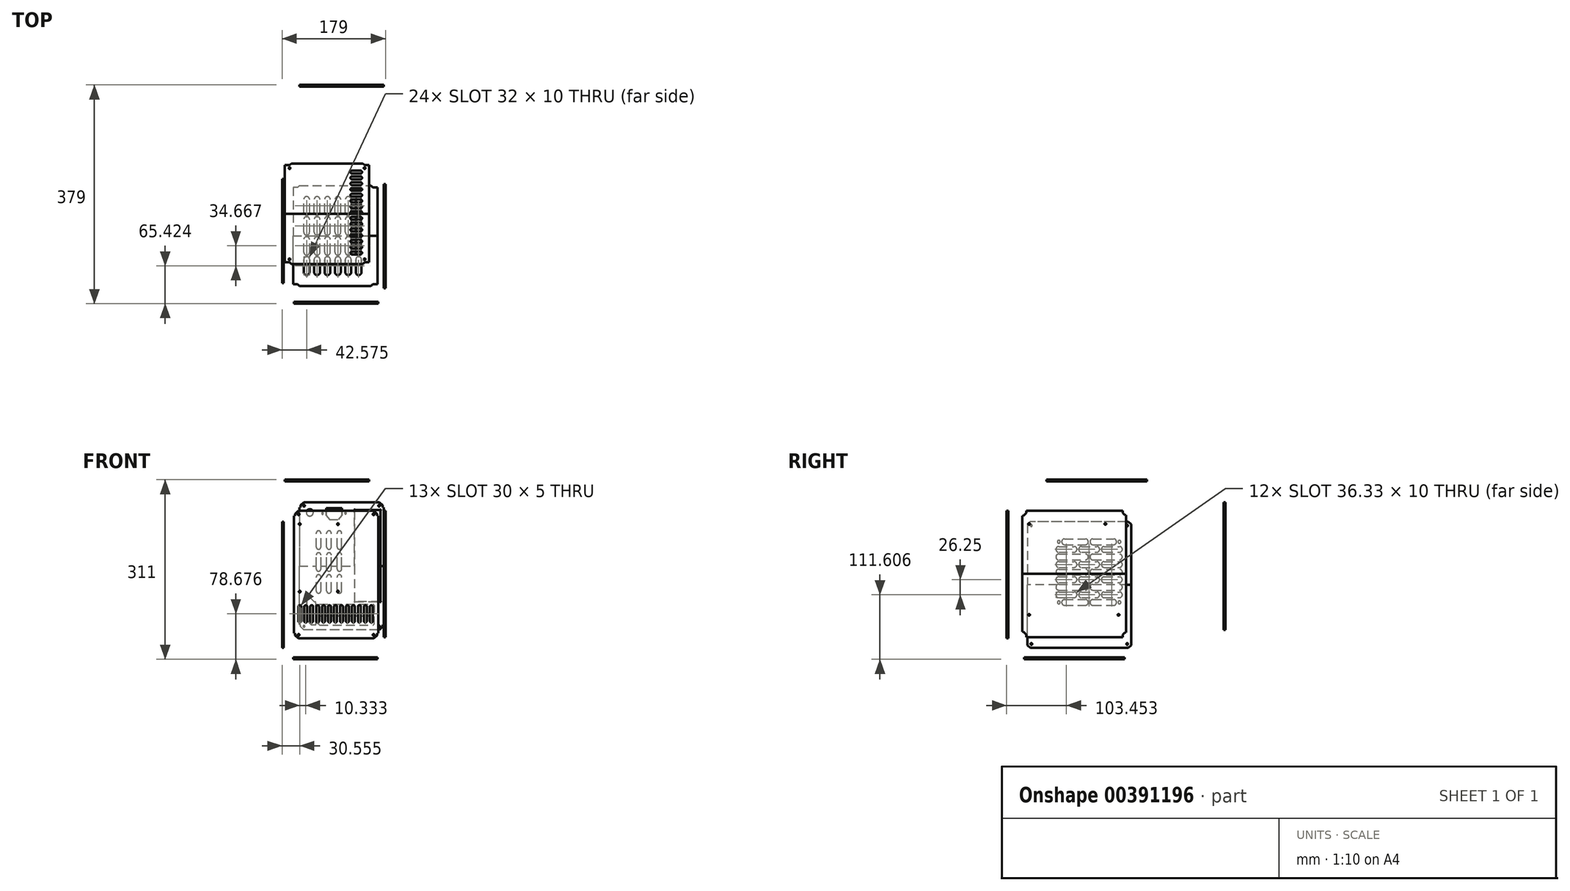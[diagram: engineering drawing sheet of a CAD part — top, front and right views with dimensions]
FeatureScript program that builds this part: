
annotation { "Feature Type Name" : "Feature", "Feature Type Description" : "" }
export const myFeature = defineFeature(function(context is Context, id is Id, definition is map)
    precondition{}
    {
        {
            var Q0;
            Q0=qCreatedBy(makeId("Front.planeOp"),FACE);
            var sketch = newSketch(context, id + "F0", { "sketchPlane" : qUnion([Q0])});
            skLineSegment(sketch, "E0.bottom", {"start": v(-75.44, 106.18) * mm, "end": v(70.56, 106.18) * mm});
            skLineSegment(sketch, "E0.top", {"start": v(-75.44, -6.32) * mm, "end": v(70.56, -6.32) * mm});
            skLineSegment(sketch, "E0.left", {"start": v(-75.44, 106.18) * mm, "end": v(-75.44, -6.32) * mm});
            skLineSegment(sketch, "E0.right", {"start": v(70.56, 106.18) * mm, "end": v(70.56, -6.32) * mm});
            skLineSegment(sketch, "E1", {"start": v(-73.44, 98.68) * mm, "end": v(-67.94, 104.18) * mm});
            skLineSegment(sketch, "E2", {"start": v(63.06, 104.18) * mm, "end": v(-67.94, 104.18) * mm});
            skLineSegment(sketch, "E3", {"start": v(63.06, 104.18) * mm, "end": v(68.56, 98.68) * mm});
            skLineSegment(sketch, "E4", {"start": v(-75.44, 98.18) * mm, "end": v(-67.44, 98.18) * mm, "construction": true});
            skCircle(sketch, "E5", {"center": v(-67.44, 98.18) * mm, "radius": 1.5 * mm});
            skLineSegment(sketch, "E6", {"start": v(70.56, 98.18) * mm, "end": v(62.56, 98.18) * mm, "construction": true});
            skCircle(sketch, "E7", {"center": v(62.56, 98.18) * mm, "radius": 1.5 * mm});
            skLineSegment(sketch, "E8", {"start": v(-73.44, 98.68) * mm, "end": v(-73.44, 95.18) * mm});
            skLineSegment(sketch, "E9", {"start": v(-73.44, 95.18) * mm, "end": v(-75.44, 95.18) * mm});
            skLineSegment(sketch, "E10", {"start": v(68.56, 98.68) * mm, "end": v(68.56, 95.18) * mm});
            skLineSegment(sketch, "E11", {"start": v(68.56, 95.18) * mm, "end": v(70.56, 95.18) * mm});
            skLineSegment(sketch, "E12", {"start": v(63.06, 104.18) * mm, "end": v(63.06, 106.18) * mm, "construction": true});
            skSolve(sketch);
        }
        {
            var Q0;
            {var subQ1=sQuery(id+"F0.wireOp",EDGE,"E0.top");Q0=makeQuery(id+"F0.imprint","IMPRINT",FACE,{"disambiguationData":[TD([[makeQuery(id+"F0.imprint","IMPRINT",EDGE,{"derivedFrom":subQ1}),1.0]])]});}
            extrude(context, id + "F1", {"entities" : qUnion([Q0]), "depth" : 3 * mm});
        }
        {
            var Q0;
            Q0=makeQuery(id+"F1.opExtrude","SWEPT_BODY",BODY,{"disambiguationData":[OSD([sQuery(id+"F0.wireOp",EDGE,"E0.bottom"),sQuery(id+"F0.wireOp",EDGE,"E0.top"),sQuery(id+"F0.wireOp",EDGE,"E0.left"),sQuery(id+"F0.wireOp",EDGE,"E0.right"),sQuery(id+"F0.wireOp",EDGE,"f4ycc0LQ-zHDD-6vh2-nqyr-j4wCRgx8H2At"),sQuery(id+"F0.wireOp",EDGE,"E1"),sQuery(id+"F0.wireOp",EDGE,"8kIEKiAh-QTEb-dtpp-JcTS-wpPMPQfBbqQd"),sQuery(id+"F0.wireOp",EDGE,"IAD0FTGy-GJaP-wMLm-guci-XfnhwucHu2uu"),sQuery(id+"F0.wireOp",EDGE,"IvHsRxJE-VIxi-RXbs-pRJC-tqeUj7lQNFDg"),sQuery(id+"F0.wireOp",EDGE,"jDx6nEBO-jJHg-Gf5S-wIms-nsZNRVFYcTxt")])]});
            var Q1;
            Q1=makeQuery(id+"F1.opExtrude","SWEPT_FACE",FACE,{"disambiguationData":[OSD([sQuery(id+"F0.wireOp",EDGE,"E0.top")])]});
            mirror(context, id + "F2", {"operationType" : NewBodyOperationType.ADD, "entities" : qUnion([Q0]), "mirrorPlane" : qUnion([Q1])});
        }
        {
            var Q0;
            {var subQ0=makeQuery(id+"F1.opExtrude","CAP_FACE",FACE,{"disambiguationData":[OSD([sQuery(id+"F0.wireOp",EDGE,"E0.bottom"),sQuery(id+"F0.wireOp",EDGE,"E0.top"),sQuery(id+"F0.wireOp",EDGE,"E0.left"),sQuery(id+"F0.wireOp",EDGE,"E0.right"),sQuery(id+"F0.wireOp",EDGE,"f4ycc0LQ-zHDD-6vh2-nqyr-j4wCRgx8H2At"),sQuery(id+"F0.wireOp",EDGE,"E1"),sQuery(id+"F0.wireOp",EDGE,"8kIEKiAh-QTEb-dtpp-JcTS-wpPMPQfBbqQd"),sQuery(id+"F0.wireOp",EDGE,"IAD0FTGy-GJaP-wMLm-guci-XfnhwucHu2uu"),sQuery(id+"F0.wireOp",EDGE,"IvHsRxJE-VIxi-RXbs-pRJC-tqeUj7lQNFDg"),sQuery(id+"F0.wireOp",EDGE,"jDx6nEBO-jJHg-Gf5S-wIms-nsZNRVFYcTxt")])],"isStart":false});Q0=makeQuery(id+"F2.boolean.opBoolean","MERGE",FACE,{"derivedFrom":[subQ0,makeQuery(id+"F2.opPattern","COPY",FACE,{"derivedFrom":subQ0,"instanceName":"1"})]});}
            var sketch = newSketch(context, id + "F3", { "sketchPlane" : qUnion([Q0])});
            skLineSegment(sketch, "E13", {"start": v(-65.44, -86.82) * mm, "end": v(-65.44, -116.82) * mm, "construction": true});
            skLineSegment(sketch, "E14.bottom", {"start": v(-65.44, 81.18) * mm, "end": v(0.76, 81.18) * mm, "construction": true});
            skLineSegment(sketch, "E14.top", {"start": v(-65.44, -35.82) * mm, "end": v(0.76, -35.82) * mm, "construction": true});
            skLineSegment(sketch, "E14.left", {"start": v(-65.44, 81.18) * mm, "end": v(-65.44, -35.82) * mm, "construction": true});
            skLineSegment(sketch, "E14.right", {"start": v(0.76, 81.18) * mm, "end": v(0.76, -35.82) * mm, "construction": true});
            skLineSegment(sketch, "E15", {"start": v(-65.44, 81.18) * mm, "end": v(-75.44, 81.18) * mm, "construction": true});
            skCircle(sketch, "E16", {"center": v(0.76, 81.18) * mm, "radius": 1.5 * mm});
            skCircle(sketch, "E17", {"center": v(-65.44, 81.18) * mm, "radius": 1.5 * mm});
            skCircle(sketch, "E18", {"center": v(-65.44, -35.82) * mm, "radius": 1.5 * mm});
            skCircle(sketch, "E19", {"center": v(0.76, -35.82) * mm, "radius": 1.5 * mm});
            skLineSegment(sketch, "E20", {"start": v(-65.44, -86.82) * mm, "end": v(-65.44, -61.82) * mm, "construction": true});
            skArc(sketch, "E21.0.startCap", {"start": v(-62.94, -86.82) * mm, "mid": v(-65.44, -89.32) * mm, "end": v(-67.94, -86.82) * mm});
            skArc(sketch, "E21.0.endCap", {"start": v(-67.94, -61.82) * mm, "mid": v(-65.44, -59.32) * mm, "end": v(-62.94, -61.82) * mm});
            skLineSegment(sketch, "E21.0.left", {"start": v(-67.94, -86.82) * mm, "end": v(-67.94, -61.82) * mm});
            skLineSegment(sketch, "E21.0.right", {"start": v(-62.94, -86.82) * mm, "end": v(-62.94, -61.82) * mm});
            skLineSegment(sketch, "E22.1.0.0", {"start": v(-55.11, -86.82) * mm, "end": v(-55.11, -61.82) * mm, "construction": true});
            skArc(sketch, "E22.1.0.1", {"start": v(-52.61, -86.82) * mm, "mid": v(-55.11, -89.32) * mm, "end": v(-57.61, -86.82) * mm});
            skArc(sketch, "E22.1.0.2", {"start": v(-57.61, -61.82) * mm, "mid": v(-55.11, -59.32) * mm, "end": v(-52.61, -61.82) * mm});
            skLineSegment(sketch, "E22.1.0.3", {"start": v(-52.61, -86.82) * mm, "end": v(-52.61, -61.82) * mm});
            skLineSegment(sketch, "E22.1.0.4", {"start": v(-57.61, -86.82) * mm, "end": v(-57.61, -61.82) * mm});
            skLineSegment(sketch, "E22.2.0.0", {"start": v(-44.78, -86.82) * mm, "end": v(-44.78, -61.82) * mm, "construction": true});
            skArc(sketch, "E22.2.0.1", {"start": v(-42.28, -86.82) * mm, "mid": v(-44.78, -89.32) * mm, "end": v(-47.28, -86.82) * mm});
            skArc(sketch, "E22.2.0.2", {"start": v(-47.28, -61.82) * mm, "mid": v(-44.78, -59.32) * mm, "end": v(-42.28, -61.82) * mm});
            skLineSegment(sketch, "E22.2.0.3", {"start": v(-42.28, -86.82) * mm, "end": v(-42.28, -61.82) * mm});
            skLineSegment(sketch, "E22.2.0.4", {"start": v(-47.28, -86.82) * mm, "end": v(-47.28, -61.82) * mm});
            skLineSegment(sketch, "E22.3.0.0", {"start": v(-34.45, -86.82) * mm, "end": v(-34.45, -61.82) * mm, "construction": true});
            skArc(sketch, "E22.3.0.1", {"start": v(-31.95, -86.82) * mm, "mid": v(-34.45, -89.32) * mm, "end": v(-36.95, -86.82) * mm});
            skArc(sketch, "E22.3.0.2", {"start": v(-36.95, -61.82) * mm, "mid": v(-34.45, -59.32) * mm, "end": v(-31.95, -61.82) * mm});
            skLineSegment(sketch, "E22.3.0.3", {"start": v(-31.95, -86.82) * mm, "end": v(-31.95, -61.82) * mm});
            skLineSegment(sketch, "E22.3.0.4", {"start": v(-36.95, -86.82) * mm, "end": v(-36.95, -61.82) * mm});
            skLineSegment(sketch, "E22.4.0.0", {"start": v(-24.11, -86.82) * mm, "end": v(-24.11, -61.82) * mm, "construction": true});
            skArc(sketch, "E22.4.0.1", {"start": v(-21.61, -86.82) * mm, "mid": v(-24.11, -89.32) * mm, "end": v(-26.61, -86.82) * mm});
            skArc(sketch, "E22.4.0.2", {"start": v(-26.61, -61.82) * mm, "mid": v(-24.11, -59.32) * mm, "end": v(-21.61, -61.82) * mm});
            skLineSegment(sketch, "E22.4.0.3", {"start": v(-21.61, -86.82) * mm, "end": v(-21.61, -61.82) * mm});
            skLineSegment(sketch, "E22.4.0.4", {"start": v(-26.61, -86.82) * mm, "end": v(-26.61, -61.82) * mm});
            skLineSegment(sketch, "E22.5.0.0", {"start": v(-13.78, -86.82) * mm, "end": v(-13.78, -61.82) * mm, "construction": true});
            skArc(sketch, "E22.5.0.1", {"start": v(-11.28, -86.82) * mm, "mid": v(-13.78, -89.32) * mm, "end": v(-16.28, -86.82) * mm});
            skArc(sketch, "E22.5.0.2", {"start": v(-16.28, -61.82) * mm, "mid": v(-13.78, -59.32) * mm, "end": v(-11.28, -61.82) * mm});
            skLineSegment(sketch, "E22.5.0.3", {"start": v(-11.28, -86.82) * mm, "end": v(-11.28, -61.82) * mm});
            skLineSegment(sketch, "E22.5.0.4", {"start": v(-16.28, -86.82) * mm, "end": v(-16.28, -61.82) * mm});
            skLineSegment(sketch, "E22.6.0.0", {"start": v(-3.45, -86.82) * mm, "end": v(-3.45, -61.82) * mm, "construction": true});
            skArc(sketch, "E22.6.0.1", {"start": v(-0.95, -86.82) * mm, "mid": v(-3.45, -89.32) * mm, "end": v(-5.95, -86.82) * mm});
            skArc(sketch, "E22.6.0.2", {"start": v(-5.95, -61.82) * mm, "mid": v(-3.45, -59.32) * mm, "end": v(-0.95, -61.82) * mm});
            skLineSegment(sketch, "E22.6.0.3", {"start": v(-0.95, -86.82) * mm, "end": v(-0.95, -61.82) * mm});
            skLineSegment(sketch, "E22.6.0.4", {"start": v(-5.95, -86.82) * mm, "end": v(-5.95, -61.82) * mm});
            skLineSegment(sketch, "E22.7.0.0", {"start": v(6.89, -86.82) * mm, "end": v(6.89, -61.82) * mm, "construction": true});
            skArc(sketch, "E22.7.0.1", {"start": v(9.39, -86.82) * mm, "mid": v(6.89, -89.32) * mm, "end": v(4.39, -86.82) * mm});
            skArc(sketch, "E22.7.0.2", {"start": v(4.39, -61.82) * mm, "mid": v(6.89, -59.32) * mm, "end": v(9.39, -61.82) * mm});
            skLineSegment(sketch, "E22.7.0.3", {"start": v(9.39, -86.82) * mm, "end": v(9.39, -61.82) * mm});
            skLineSegment(sketch, "E22.7.0.4", {"start": v(4.39, -86.82) * mm, "end": v(4.39, -61.82) * mm});
            skLineSegment(sketch, "E22.8.0.0", {"start": v(17.22, -86.82) * mm, "end": v(17.22, -61.82) * mm, "construction": true});
            skArc(sketch, "E22.8.0.1", {"start": v(19.72, -86.82) * mm, "mid": v(17.22, -89.32) * mm, "end": v(14.72, -86.82) * mm});
            skArc(sketch, "E22.8.0.2", {"start": v(14.72, -61.82) * mm, "mid": v(17.22, -59.32) * mm, "end": v(19.72, -61.82) * mm});
            skLineSegment(sketch, "E22.8.0.3", {"start": v(19.72, -86.82) * mm, "end": v(19.72, -61.82) * mm});
            skLineSegment(sketch, "E22.8.0.4", {"start": v(14.72, -86.82) * mm, "end": v(14.72, -61.82) * mm});
            skLineSegment(sketch, "E22.9.0.0", {"start": v(27.55, -86.82) * mm, "end": v(27.55, -61.82) * mm, "construction": true});
            skArc(sketch, "E22.9.0.1", {"start": v(30.05, -86.82) * mm, "mid": v(27.55, -89.32) * mm, "end": v(25.05, -86.82) * mm});
            skArc(sketch, "E22.9.0.2", {"start": v(25.05, -61.82) * mm, "mid": v(27.55, -59.32) * mm, "end": v(30.05, -61.82) * mm});
            skLineSegment(sketch, "E22.9.0.3", {"start": v(30.05, -86.82) * mm, "end": v(30.05, -61.82) * mm});
            skLineSegment(sketch, "E22.9.0.4", {"start": v(25.05, -86.82) * mm, "end": v(25.05, -61.82) * mm});
            skLineSegment(sketch, "E22.10.0.0", {"start": v(37.89, -86.82) * mm, "end": v(37.89, -61.82) * mm, "construction": true});
            skArc(sketch, "E22.10.0.1", {"start": v(40.39, -86.82) * mm, "mid": v(37.89, -89.32) * mm, "end": v(35.39, -86.82) * mm});
            skArc(sketch, "E22.10.0.2", {"start": v(35.39, -61.82) * mm, "mid": v(37.89, -59.32) * mm, "end": v(40.39, -61.82) * mm});
            skLineSegment(sketch, "E22.10.0.3", {"start": v(40.39, -86.82) * mm, "end": v(40.39, -61.82) * mm});
            skLineSegment(sketch, "E22.10.0.4", {"start": v(35.39, -86.82) * mm, "end": v(35.39, -61.82) * mm});
            skLineSegment(sketch, "E22.11.0.0", {"start": v(48.22, -86.82) * mm, "end": v(48.22, -61.82) * mm, "construction": true});
            skArc(sketch, "E22.11.0.1", {"start": v(50.72, -86.82) * mm, "mid": v(48.22, -89.32) * mm, "end": v(45.72, -86.82) * mm});
            skArc(sketch, "E22.11.0.2", {"start": v(45.72, -61.82) * mm, "mid": v(48.22, -59.32) * mm, "end": v(50.72, -61.82) * mm});
            skLineSegment(sketch, "E22.11.0.3", {"start": v(50.72, -86.82) * mm, "end": v(50.72, -61.82) * mm});
            skLineSegment(sketch, "E22.11.0.4", {"start": v(45.72, -86.82) * mm, "end": v(45.72, -61.82) * mm});
            skLineSegment(sketch, "E22.12.0.0", {"start": v(58.55, -86.82) * mm, "end": v(58.55, -61.82) * mm, "construction": true});
            skArc(sketch, "E22.12.0.1", {"start": v(61.05, -86.82) * mm, "mid": v(58.55, -89.32) * mm, "end": v(56.05, -86.82) * mm});
            skArc(sketch, "E22.12.0.2", {"start": v(56.05, -61.82) * mm, "mid": v(58.55, -59.32) * mm, "end": v(61.05, -61.82) * mm});
            skLineSegment(sketch, "E22.12.0.3", {"start": v(61.05, -86.82) * mm, "end": v(61.05, -61.82) * mm});
            skLineSegment(sketch, "E22.12.0.4", {"start": v(56.05, -86.82) * mm, "end": v(56.05, -61.82) * mm});
            skLineSegment(sketch, "E22.direction1", {"start": v(-67.94, -86.82) * mm, "end": v(-57.61, -86.82) * mm, "construction": true});
            skSolve(sketch);
        }
        {
            var Q0;
            Q0=qSketchRegion(id+"F3",true);
            extrude(context, id + "F4", {"entities" : qUnion([Q0]), "operationType" : NewBodyOperationType.REMOVE, "oppositeDirection" : true, "depth" : 3 * mm});
        }
        {
            var Q0;
            Q0=qCreatedBy(makeId("Right.planeOp"),FACE);
            cPlane(context, id + "F5", {"entities" : qUnion([Q0]), "cplaneType" : CPlaneType.OFFSET, "offset" : 80 * mm, "width" : 150 * mm, "height" : 150 * mm});
        }
        {
            var Q0;
            Q0=qCreatedBy(id+"F5.planeOp",FACE);
            var sketch = newSketch(context, id + "F6", { "sketchPlane" : qUnion([Q0])});
            skLineSegment(sketch, "E23.bottom", {"start": v(23.92, 104.5) * mm, "end": v(203.92, 104.5) * mm});
            skLineSegment(sketch, "E23.top", {"start": v(23.92, -5) * mm, "end": v(203.92, -5) * mm});
            skLineSegment(sketch, "E23.left", {"start": v(23.92, 104.5) * mm, "end": v(23.92, -5) * mm});
            skLineSegment(sketch, "E23.right", {"start": v(203.92, 104.5) * mm, "end": v(203.92, -5) * mm});
            skLineSegment(sketch, "E24", {"start": v(23.92, 95.5) * mm, "end": v(25.92, 95.5) * mm});
            skLineSegment(sketch, "E25", {"start": v(25.92, 95.5) * mm, "end": v(30.92, 100.5) * mm});
            skLineSegment(sketch, "E26", {"start": v(30.92, 100.5) * mm, "end": v(30.92, 104.5) * mm});
            skLineSegment(sketch, "E27", {"start": v(197.92, 104.5) * mm, "end": v(197.92, 100.5) * mm});
            skLineSegment(sketch, "E28", {"start": v(197.92, 100.5) * mm, "end": v(201.92, 96.5) * mm});
            skLineSegment(sketch, "E29", {"start": v(201.92, 96.5) * mm, "end": v(203.92, 96.5) * mm});
            skSolve(sketch);
        }
        {
            var Q0;
            {var subQ4=sQuery(id+"F6.wireOp",EDGE,"E23.top");Q0=makeQuery(id+"F6.imprint","IMPRINT",FACE,{"disambiguationData":[TD([[makeQuery(id+"F6.imprint","IMPRINT",EDGE,{"derivedFrom":subQ4}),1.0]])]});}
            extrude(context, id + "F7", {"entities" : qUnion([Q0]), "depth" : 3 * mm});
        }
        {
            var Q0;
            Q0=makeQuery(id+"F7.opExtrude","SWEPT_BODY",BODY,{"disambiguationData":[OSD([sQuery(id+"F6.wireOp",EDGE,"E23.bottom"),sQuery(id+"F6.wireOp",EDGE,"E23.top"),sQuery(id+"F6.wireOp",EDGE,"E23.left"),sQuery(id+"F6.wireOp",EDGE,"E23.right"),sQuery(id+"F6.wireOp",EDGE,"uhohLnhp-hqEh-HnCf-sw5P-UAyFwgDYjcBT"),sQuery(id+"F6.wireOp",EDGE,"PZ9vbapj-Vyhe-IVd5-wSIB-ihSb0FTefDFo"),sQuery(id+"F6.wireOp",EDGE,"Vy2RlQAS-aQ6k-OJzX-lqoE-WAFZ4NoHzz8E"),sQuery(id+"F6.wireOp",EDGE,"uOpGianr-bHoC-LPpd-ZrnQ-WT6fRq75YZDk"),sQuery(id+"F6.wireOp",EDGE,"ByD4MoDk-9vtG-w2Bj-nV2I-deXss6nWGu8L"),sQuery(id+"F6.wireOp",EDGE,"dErzSW6J-HGX5-GNXE-lozc-OmhnMsFbACEc"),sQuery(id+"F6.wireOp",EDGE,"oiYVu7ST-duG0-g5FE-uATR-zlAqLM0uh895"),sQuery(id+"F6.wireOp",EDGE,"fhnCciFL-T4Vn-rBCZ-nkKt-uSig2OXv9zq8")])]});
            var Q1;
            Q1=makeQuery(id+"F7.opExtrude","SWEPT_FACE",FACE,{"disambiguationData":[OSD([sQuery(id+"F6.wireOp",EDGE,"E23.top")])]});
            mirror(context, id + "F8", {"operationType" : NewBodyOperationType.ADD, "entities" : qUnion([Q0]), "mirrorPlane" : qUnion([Q1])});
        }
        {
            var Q0;
            {var subQ0=makeQuery(id+"F7.opExtrude","CAP_FACE",FACE,{"disambiguationData":[OSD([sQuery(id+"F6.wireOp",EDGE,"E23.bottom"),sQuery(id+"F6.wireOp",EDGE,"E23.top"),sQuery(id+"F6.wireOp",EDGE,"E23.left"),sQuery(id+"F6.wireOp",EDGE,"E23.right"),sQuery(id+"F6.wireOp",EDGE,"g6LnxF4V-R5jx-aabO-tbI6-ip1Ci8vFljjD"),sQuery(id+"F6.wireOp",EDGE,"agJmLhdB-riTp-nQB3-38GJ-uXkWwZ3pCfX2")])],"isStart":true});Q0=makeQuery(id+"F8.boolean.opBoolean","MERGE",FACE,{"derivedFrom":[subQ0,makeQuery(id+"F8.opPattern","COPY",FACE,{"derivedFrom":subQ0,"instanceName":"1"})]});}
            var sketch = newSketch(context, id + "F9", { "sketchPlane" : qUnion([Q0])});
            skLineSegment(sketch, "E30", {"start": v(-200.92, -82.5) * mm, "end": v(-200.92, 87.5) * mm, "construction": true});
            skLineSegment(sketch, "E31", {"start": v(-200.92, -82.5) * mm, "end": v(-30.92, -82.5) * mm, "construction": true});
            skLineSegment(sketch, "E32", {"start": v(-200.92, 87.5) * mm, "end": v(-30.92, 87.5) * mm, "construction": true});
            skLineSegment(sketch, "E33", {"start": v(-30.92, 87.5) * mm, "end": v(-30.92, -82.5) * mm, "construction": true});
            skLineSegment(sketch, "E34", {"start": v(-200.92, -76.1) * mm, "end": v(-190.72, -76.1) * mm, "construction": true});
            skCircle(sketch, "E35", {"center": v(-190.72, -76.1) * mm, "radius": 1.5 * mm});
            skLineSegment(sketch, "E36", {"start": v(-190.72, -76.1) * mm, "end": v(-35.82, -76.1) * mm, "construction": true});
            skCircle(sketch, "E37", {"center": v(-35.82, -76.1) * mm, "radius": 1.5 * mm});
            skLineSegment(sketch, "E38", {"start": v(-200.92, 81.3) * mm, "end": v(-167.92, 81.3) * mm, "construction": true});
            skCircle(sketch, "E39", {"center": v(-167.92, 81.3) * mm, "radius": 1.5 * mm});
            skLineSegment(sketch, "E40", {"start": v(-167.92, 81.3) * mm, "end": v(-35.82, 81.3) * mm, "construction": true});
            skCircle(sketch, "E41", {"center": v(-35.82, 81.3) * mm, "radius": 1.5 * mm});
            skSolve(sketch);
        }
        {
            var Q0;
            Q0=qSketchRegion(id+"F9",true);
            var Q1;
            {var subQ0=sQuery(id+"F9.wireOp",EDGE,"b6TVsvgF-kPWZ-6Ni7-LZi2-MRGtpnM4VBQ9");Q1=makeQuery(id+"F9.imprint","IMPRINT",FACE,{"disambiguationData":[TD([[makeQuery(id+"F9.imprint","IMPRINT",EDGE,{"derivedFrom":subQ0}),-1.0]])]});}
            extrude(context, id + "F10", {"entities" : qUnion([Q0, Q1]), "operationType" : NewBodyOperationType.REMOVE, "oppositeDirection" : true, "depth" : 25 * mm});
        }
        {
            var Q0;
            Q0=qCreatedBy(makeId("Right.planeOp"),FACE);
            cPlane(context, id + "F11", {"entities" : qUnion([Q0]), "cplaneType" : CPlaneType.OFFSET, "offset" : 96 * mm, "oppositeDirection" : true, "width" : 150 * mm, "height" : 150 * mm});
        }
        {
            var Q0;
            Q0=qCreatedBy(id+"F11.planeOp",FACE);
            var sketch = newSketch(context, id + "F12", { "sketchPlane" : qUnion([Q0])});
            skLineSegment(sketch, "E42.bottom", {"start": v(212.79, 85.48) * mm, "end": v(32.79, 85.48) * mm});
            skLineSegment(sketch, "E42.top", {"start": v(212.79, -24.02) * mm, "end": v(32.79, -24.02) * mm});
            skLineSegment(sketch, "E42.left", {"start": v(212.79, 85.48) * mm, "end": v(212.79, -24.02) * mm});
            skLineSegment(sketch, "E42.right", {"start": v(32.79, 85.48) * mm, "end": v(32.79, -24.02) * mm});
            skLineSegment(sketch, "E43", {"start": v(212.79, 80.48) * mm, "end": v(207.79, 85.48) * mm});
            skLineSegment(sketch, "E44", {"start": v(37.79, 85.48) * mm, "end": v(32.79, 80.48) * mm});
            skLineSegment(sketch, "E45", {"start": v(212.79, 78.48) * mm, "end": v(205.79, 78.48) * mm, "construction": true});
            skCircle(sketch, "E46", {"center": v(205.79, 78.48) * mm, "radius": 1.5 * mm});
            skLineSegment(sketch, "E47", {"start": v(32.79, 78.48) * mm, "end": v(39.79, 78.48) * mm, "construction": true});
            skCircle(sketch, "E48", {"center": v(39.79, 78.48) * mm, "radius": 1.5 * mm});
            skSolve(sketch);
        }
        {
            var Q0;
            {var subQ1=sQuery(id+"F12.wireOp",EDGE,"E42.top");Q0=makeQuery(id+"F12.imprint","IMPRINT",FACE,{"disambiguationData":[TD([[makeQuery(id+"F12.imprint","IMPRINT",EDGE,{"derivedFrom":subQ1}),-1.0]])]});}
            extrude(context, id + "F13", {"entities" : qUnion([Q0]), "depth" : 3 * mm});
        }
        {
            var Q0;
            Q0=makeQuery(id+"F13.opExtrude","SWEPT_BODY",BODY,{"disambiguationData":[OSD([sQuery(id+"F12.wireOp",EDGE,"E42.bottom"),sQuery(id+"F12.wireOp",EDGE,"E42.top"),sQuery(id+"F12.wireOp",EDGE,"E42.left"),sQuery(id+"F12.wireOp",EDGE,"E42.right"),sQuery(id+"F12.wireOp",EDGE,"E43"),sQuery(id+"F12.wireOp",EDGE,"E44")])]});
            var Q1;
            Q1=makeQuery(id+"F13.opExtrude","SWEPT_FACE",FACE,{"disambiguationData":[OSD([sQuery(id+"F12.wireOp",EDGE,"E42.top")])]});
            mirror(context, id + "F14", {"operationType" : NewBodyOperationType.ADD, "entities" : qUnion([Q0]), "mirrorPlane" : qUnion([Q1])});
        }
        {
            var Q0;
            {var subQ0=makeQuery(id+"F13.opExtrude","CAP_FACE",FACE,{"disambiguationData":[OSD([sQuery(id+"F12.wireOp",EDGE,"E42.bottom"),sQuery(id+"F12.wireOp",EDGE,"E42.top"),sQuery(id+"F12.wireOp",EDGE,"E42.left"),sQuery(id+"F12.wireOp",EDGE,"E42.right"),sQuery(id+"F12.wireOp",EDGE,"E43"),sQuery(id+"F12.wireOp",EDGE,"E44")])],"isStart":true});Q0=makeQuery(id+"F14.boolean.opBoolean","MERGE",FACE,{"derivedFrom":[subQ0,makeQuery(id+"F14.opPattern","COPY",FACE,{"derivedFrom":subQ0,"instanceName":"1"})]});}
            var sketch = newSketch(context, id + "F15", { "sketchPlane" : qUnion([Q0])});
            skLineSegment(sketch, "E49", {"start": v(-212.79, 55.48) * mm, "end": v(-192.29, 55.48) * mm, "construction": true});
            skLineSegment(sketch, "E50", {"start": v(-192.29, 55.48) * mm, "end": v(-192.29, -59.52) * mm, "construction": true});
            skLineSegment(sketch, "E51", {"start": v(-192.29, 50.48) * mm, "end": v(-182.29, 50.48) * mm, "construction": true});
            skLineSegment(sketch, "E52", {"start": v(-182.29, 50.48) * mm, "end": v(-146.29, 50.48) * mm, "construction": true});
            skLineSegment(sketch, "E53", {"start": v(-192.29, 37.36) * mm, "end": v(-165.95, 37.36) * mm, "construction": true});
            skLineSegment(sketch, "E54", {"start": v(-192.29, 24.23) * mm, "end": v(-146.29, 24.23) * mm, "construction": true});
            skLineSegment(sketch, "E55", {"start": v(-192.29, 11.1) * mm, "end": v(-165.95, 11.1) * mm, "construction": true});
            skLineSegment(sketch, "E56", {"start": v(-192.29, -2.02) * mm, "end": v(-146.29, -2.02) * mm, "construction": true});
            skLineSegment(sketch, "E57", {"start": v(-192.29, -15.14) * mm, "end": v(-165.95, -15.14) * mm, "construction": true});
            skLineSegment(sketch, "E58", {"start": v(-192.29, -28.27) * mm, "end": v(-146.29, -28.27) * mm, "construction": true});
            skLineSegment(sketch, "E59", {"start": v(-192.29, -41.4) * mm, "end": v(-165.95, -41.4) * mm, "construction": true});
            skLineSegment(sketch, "E60", {"start": v(-192.29, -54.52) * mm, "end": v(-182.29, -54.52) * mm, "construction": true});
            skLineSegment(sketch, "E61", {"start": v(-182.29, -54.52) * mm, "end": v(-146.29, -54.52) * mm, "construction": true});
            skCircle(sketch, "E62", {"center": v(-192.29, 50.48) * mm, "radius": 2.5 * mm});
            skLineSegment(sketch, "E63", {"start": v(-97.29, 50.48) * mm, "end": v(-87.29, 50.48) * mm, "construction": true});
            skPoint(sketch, "E63.endSnap0", {"position": v(-82.69, 50.48) * mm});
            skCircle(sketch, "E64", {"center": v(-87.29, 50.48) * mm, "radius": 2.5 * mm});
            skLineSegment(sketch, "E65", {"start": v(-146.29, 50.48) * mm, "end": v(-133.29, 50.48) * mm, "construction": true});
            skLineSegment(sketch, "E66", {"start": v(-133.29, 50.48) * mm, "end": v(-97.29, 50.48) * mm, "construction": true});
            skArc(sketch, "E67.0.startCap", {"start": v(-182.29, 45.48) * mm, "mid": v(-187.29, 50.48) * mm, "end": v(-182.29, 55.48) * mm});
            skArc(sketch, "E67.0.endCap", {"start": v(-146.29, 55.48) * mm, "mid": v(-141.29, 50.48) * mm, "end": v(-146.29, 45.48) * mm});
            skLineSegment(sketch, "E67.0.left", {"start": v(-182.29, 55.48) * mm, "end": v(-146.29, 55.48) * mm});
            skLineSegment(sketch, "E67.0.right", {"start": v(-182.29, 45.48) * mm, "end": v(-146.29, 45.48) * mm});
            skArc(sketch, "E67.1.startCap", {"start": v(-133.29, 45.48) * mm, "mid": v(-138.29, 50.48) * mm, "end": v(-133.29, 55.48) * mm});
            skArc(sketch, "E67.1.endCap", {"start": v(-97.29, 55.48) * mm, "mid": v(-92.29, 50.48) * mm, "end": v(-97.29, 45.48) * mm});
            skLineSegment(sketch, "E67.1.left", {"start": v(-133.29, 55.48) * mm, "end": v(-97.29, 55.48) * mm});
            skLineSegment(sketch, "E67.1.right", {"start": v(-133.29, 45.48) * mm, "end": v(-97.29, 45.48) * mm});
            skLineSegment(sketch, "E68", {"start": v(-165.95, 37.36) * mm, "end": v(-152.95, 37.36) * mm, "construction": true});
            skLineSegment(sketch, "E69", {"start": v(-152.95, 37.36) * mm, "end": v(-126.62, 37.36) * mm, "construction": true});
            skLineSegment(sketch, "E70", {"start": v(-126.62, 37.36) * mm, "end": v(-113.62, 37.36) * mm, "construction": true});
            skLineSegment(sketch, "E71", {"start": v(-113.62, 37.36) * mm, "end": v(-87.29, 37.36) * mm, "construction": true});
            skArc(sketch, "E72.0.startCap", {"start": v(-192.29, 32.36) * mm, "mid": v(-197.29, 37.36) * mm, "end": v(-192.29, 42.36) * mm});
            skArc(sketch, "E72.0.endCap", {"start": v(-165.95, 42.36) * mm, "mid": v(-160.95, 37.36) * mm, "end": v(-165.95, 32.36) * mm});
            skLineSegment(sketch, "E72.0.left", {"start": v(-192.29, 42.36) * mm, "end": v(-165.95, 42.36) * mm});
            skLineSegment(sketch, "E72.0.right", {"start": v(-192.29, 32.36) * mm, "end": v(-165.95, 32.36) * mm});
            skArc(sketch, "E72.1.startCap", {"start": v(-152.95, 32.36) * mm, "mid": v(-157.95, 37.36) * mm, "end": v(-152.95, 42.36) * mm});
            skArc(sketch, "E72.1.endCap", {"start": v(-126.62, 42.36) * mm, "mid": v(-121.62, 37.36) * mm, "end": v(-126.62, 32.36) * mm});
            skLineSegment(sketch, "E72.1.left", {"start": v(-152.95, 42.36) * mm, "end": v(-126.62, 42.36) * mm});
            skLineSegment(sketch, "E72.1.right", {"start": v(-152.95, 32.36) * mm, "end": v(-126.62, 32.36) * mm});
            skArc(sketch, "E72.2.startCap", {"start": v(-113.62, 32.36) * mm, "mid": v(-118.62, 37.36) * mm, "end": v(-113.62, 42.36) * mm});
            skArc(sketch, "E72.2.endCap", {"start": v(-87.29, 42.36) * mm, "mid": v(-82.29, 37.36) * mm, "end": v(-87.29, 32.36) * mm});
            skLineSegment(sketch, "E72.2.left", {"start": v(-113.62, 42.36) * mm, "end": v(-87.29, 42.36) * mm});
            skLineSegment(sketch, "E72.2.right", {"start": v(-113.62, 32.36) * mm, "end": v(-87.29, 32.36) * mm});
            skLineSegment(sketch, "E73", {"start": v(-146.29, 24.23) * mm, "end": v(-133.29, 24.23) * mm, "construction": true});
            skLineSegment(sketch, "E74", {"start": v(-133.29, 24.23) * mm, "end": v(-87.29, 24.23) * mm, "construction": true});
            skArc(sketch, "E75.0.startCap", {"start": v(-192.29, 19.23) * mm, "mid": v(-197.29, 24.23) * mm, "end": v(-192.29, 29.23) * mm});
            skArc(sketch, "E75.0.endCap", {"start": v(-146.29, 29.23) * mm, "mid": v(-141.29, 24.23) * mm, "end": v(-146.29, 19.23) * mm});
            skLineSegment(sketch, "E75.0.left", {"start": v(-192.29, 29.23) * mm, "end": v(-146.29, 29.23) * mm});
            skLineSegment(sketch, "E75.0.right", {"start": v(-192.29, 19.23) * mm, "end": v(-146.29, 19.23) * mm});
            skArc(sketch, "E75.1.startCap", {"start": v(-133.29, 19.23) * mm, "mid": v(-138.29, 24.23) * mm, "end": v(-133.29, 29.23) * mm});
            skArc(sketch, "E75.1.endCap", {"start": v(-87.29, 29.23) * mm, "mid": v(-82.29, 24.23) * mm, "end": v(-87.29, 19.23) * mm});
            skLineSegment(sketch, "E75.1.left", {"start": v(-133.29, 29.23) * mm, "end": v(-87.29, 29.23) * mm});
            skLineSegment(sketch, "E75.1.right", {"start": v(-133.29, 19.23) * mm, "end": v(-87.29, 19.23) * mm});
            skLineSegment(sketch, "E76", {"start": v(-165.95, 11.1) * mm, "end": v(-152.95, 11.1) * mm, "construction": true});
            skLineSegment(sketch, "E77", {"start": v(-152.95, 11.1) * mm, "end": v(-126.62, 11.1) * mm, "construction": true});
            skLineSegment(sketch, "E78", {"start": v(-126.62, 11.1) * mm, "end": v(-113.62, 11.1) * mm, "construction": true});
            skLineSegment(sketch, "E79", {"start": v(-113.62, 11.1) * mm, "end": v(-87.29, 11.1) * mm, "construction": true});
            skArc(sketch, "E80.0.startCap", {"start": v(-192.29, 6.1) * mm, "mid": v(-197.29, 11.1) * mm, "end": v(-192.29, 16.1) * mm});
            skArc(sketch, "E80.0.endCap", {"start": v(-165.95, 16.1) * mm, "mid": v(-160.95, 11.1) * mm, "end": v(-165.95, 6.1) * mm});
            skLineSegment(sketch, "E80.0.left", {"start": v(-192.29, 16.1) * mm, "end": v(-165.95, 16.1) * mm});
            skLineSegment(sketch, "E80.0.right", {"start": v(-192.29, 6.1) * mm, "end": v(-165.95, 6.1) * mm});
            skArc(sketch, "E80.1.startCap", {"start": v(-152.95, 6.1) * mm, "mid": v(-157.95, 11.1) * mm, "end": v(-152.95, 16.1) * mm});
            skArc(sketch, "E80.1.endCap", {"start": v(-126.62, 16.1) * mm, "mid": v(-121.62, 11.1) * mm, "end": v(-126.62, 6.1) * mm});
            skLineSegment(sketch, "E80.1.left", {"start": v(-152.95, 16.1) * mm, "end": v(-126.62, 16.1) * mm});
            skLineSegment(sketch, "E80.1.right", {"start": v(-152.95, 6.1) * mm, "end": v(-126.62, 6.1) * mm});
            skArc(sketch, "E80.2.startCap", {"start": v(-113.62, 6.1) * mm, "mid": v(-118.62, 11.1) * mm, "end": v(-113.62, 16.1) * mm});
            skArc(sketch, "E80.2.endCap", {"start": v(-87.29, 16.1) * mm, "mid": v(-82.29, 11.1) * mm, "end": v(-87.29, 6.1) * mm});
            skLineSegment(sketch, "E80.2.left", {"start": v(-113.62, 16.1) * mm, "end": v(-87.29, 16.1) * mm});
            skLineSegment(sketch, "E80.2.right", {"start": v(-113.62, 6.1) * mm, "end": v(-87.29, 6.1) * mm});
            skLineSegment(sketch, "E81", {"start": v(-146.29, -2.02) * mm, "end": v(-133.29, -2.02) * mm, "construction": true});
            skLineSegment(sketch, "E82", {"start": v(-133.29, -2.02) * mm, "end": v(-87.29, -2.02) * mm, "construction": true});
            skLineSegment(sketch, "E83", {"start": v(-165.95, -15.14) * mm, "end": v(-152.95, -15.14) * mm, "construction": true});
            skLineSegment(sketch, "E84", {"start": v(-152.95, -15.14) * mm, "end": v(-126.62, -15.14) * mm, "construction": true});
            skLineSegment(sketch, "E85", {"start": v(-126.62, -15.14) * mm, "end": v(-113.62, -15.14) * mm, "construction": true});
            skLineSegment(sketch, "E86", {"start": v(-113.62, -15.14) * mm, "end": v(-87.29, -15.14) * mm, "construction": true});
            skLineSegment(sketch, "E87", {"start": v(-146.29, -28.27) * mm, "end": v(-133.29, -28.27) * mm, "construction": true});
            skLineSegment(sketch, "E88", {"start": v(-133.29, -28.27) * mm, "end": v(-87.29, -28.27) * mm, "construction": true});
            skLineSegment(sketch, "E89", {"start": v(-165.95, -41.4) * mm, "end": v(-152.95, -41.4) * mm, "construction": true});
            skLineSegment(sketch, "E90", {"start": v(-152.95, -41.4) * mm, "end": v(-126.62, -41.4) * mm, "construction": true});
            skLineSegment(sketch, "E91", {"start": v(-126.62, -41.4) * mm, "end": v(-113.62, -41.4) * mm, "construction": true});
            skLineSegment(sketch, "E92", {"start": v(-113.62, -41.4) * mm, "end": v(-87.29, -41.4) * mm, "construction": true});
            skLineSegment(sketch, "E93", {"start": v(-146.29, -54.52) * mm, "end": v(-133.29, -54.52) * mm, "construction": true});
            skLineSegment(sketch, "E94", {"start": v(-133.29, -54.52) * mm, "end": v(-97.29, -54.52) * mm, "construction": true});
            skLineSegment(sketch, "E95", {"start": v(-97.29, -54.52) * mm, "end": v(-87.29, -54.52) * mm, "construction": true});
            skArc(sketch, "E96.0.startCap", {"start": v(-192.29, -7.02) * mm, "mid": v(-197.29, -2.02) * mm, "end": v(-192.29, 2.98) * mm});
            skArc(sketch, "E96.0.endCap", {"start": v(-146.29, 2.98) * mm, "mid": v(-141.29, -2.02) * mm, "end": v(-146.29, -7.02) * mm});
            skLineSegment(sketch, "E96.0.left", {"start": v(-192.29, 2.98) * mm, "end": v(-146.29, 2.98) * mm});
            skLineSegment(sketch, "E96.0.right", {"start": v(-192.29, -7.02) * mm, "end": v(-146.29, -7.02) * mm});
            skArc(sketch, "E96.1.startCap", {"start": v(-133.29, -7.02) * mm, "mid": v(-138.29, -2.02) * mm, "end": v(-133.29, 2.98) * mm});
            skArc(sketch, "E96.1.endCap", {"start": v(-87.29, 2.98) * mm, "mid": v(-82.29, -2.02) * mm, "end": v(-87.29, -7.02) * mm});
            skLineSegment(sketch, "E96.1.left", {"start": v(-133.29, 2.98) * mm, "end": v(-87.29, 2.98) * mm});
            skLineSegment(sketch, "E96.1.right", {"start": v(-133.29, -7.02) * mm, "end": v(-87.29, -7.02) * mm});
            skArc(sketch, "E96.2.startCap", {"start": v(-192.29, -20.14) * mm, "mid": v(-197.29, -15.14) * mm, "end": v(-192.29, -10.14) * mm});
            skArc(sketch, "E96.2.endCap", {"start": v(-165.95, -10.14) * mm, "mid": v(-160.95, -15.14) * mm, "end": v(-165.95, -20.14) * mm});
            skLineSegment(sketch, "E96.2.left", {"start": v(-192.29, -10.14) * mm, "end": v(-165.95, -10.14) * mm});
            skLineSegment(sketch, "E96.2.right", {"start": v(-192.29, -20.14) * mm, "end": v(-165.95, -20.14) * mm});
            skArc(sketch, "E96.3.startCap", {"start": v(-152.95, -20.14) * mm, "mid": v(-157.95, -15.14) * mm, "end": v(-152.95, -10.14) * mm});
            skArc(sketch, "E96.3.endCap", {"start": v(-126.62, -10.14) * mm, "mid": v(-121.62, -15.14) * mm, "end": v(-126.62, -20.14) * mm});
            skLineSegment(sketch, "E96.3.left", {"start": v(-152.95, -10.14) * mm, "end": v(-126.62, -10.14) * mm});
            skLineSegment(sketch, "E96.3.right", {"start": v(-152.95, -20.14) * mm, "end": v(-126.62, -20.14) * mm});
            skArc(sketch, "E96.4.startCap", {"start": v(-113.62, -20.14) * mm, "mid": v(-118.62, -15.14) * mm, "end": v(-113.62, -10.14) * mm});
            skArc(sketch, "E96.4.endCap", {"start": v(-87.29, -10.14) * mm, "mid": v(-82.29, -15.14) * mm, "end": v(-87.29, -20.14) * mm});
            skLineSegment(sketch, "E96.4.left", {"start": v(-113.62, -10.14) * mm, "end": v(-87.29, -10.14) * mm});
            skLineSegment(sketch, "E96.4.right", {"start": v(-113.62, -20.14) * mm, "end": v(-87.29, -20.14) * mm});
            skArc(sketch, "E97.0.startCap", {"start": v(-192.29, -33.27) * mm, "mid": v(-197.29, -28.27) * mm, "end": v(-192.29, -23.27) * mm});
            skArc(sketch, "E97.0.endCap", {"start": v(-146.29, -23.27) * mm, "mid": v(-141.29, -28.27) * mm, "end": v(-146.29, -33.27) * mm});
            skLineSegment(sketch, "E97.0.left", {"start": v(-192.29, -23.27) * mm, "end": v(-146.29, -23.27) * mm});
            skLineSegment(sketch, "E97.0.right", {"start": v(-192.29, -33.27) * mm, "end": v(-146.29, -33.27) * mm});
            skArc(sketch, "E97.1.startCap", {"start": v(-133.29, -33.27) * mm, "mid": v(-138.29, -28.27) * mm, "end": v(-133.29, -23.27) * mm});
            skArc(sketch, "E97.1.endCap", {"start": v(-87.29, -23.27) * mm, "mid": v(-82.29, -28.27) * mm, "end": v(-87.29, -33.27) * mm});
            skLineSegment(sketch, "E97.1.left", {"start": v(-133.29, -23.27) * mm, "end": v(-87.29, -23.27) * mm});
            skLineSegment(sketch, "E97.1.right", {"start": v(-133.29, -33.27) * mm, "end": v(-87.29, -33.27) * mm});
            skArc(sketch, "E97.2.startCap", {"start": v(-192.29, -46.4) * mm, "mid": v(-197.29, -41.4) * mm, "end": v(-192.29, -36.4) * mm});
            skArc(sketch, "E97.2.endCap", {"start": v(-165.95, -36.4) * mm, "mid": v(-160.95, -41.4) * mm, "end": v(-165.95, -46.4) * mm});
            skLineSegment(sketch, "E97.2.left", {"start": v(-192.29, -36.4) * mm, "end": v(-165.95, -36.4) * mm});
            skLineSegment(sketch, "E97.2.right", {"start": v(-192.29, -46.4) * mm, "end": v(-165.95, -46.4) * mm});
            skArc(sketch, "E97.3.startCap", {"start": v(-152.95, -46.4) * mm, "mid": v(-157.95, -41.4) * mm, "end": v(-152.95, -36.4) * mm});
            skArc(sketch, "E97.3.endCap", {"start": v(-126.62, -36.4) * mm, "mid": v(-121.62, -41.4) * mm, "end": v(-126.62, -46.4) * mm});
            skLineSegment(sketch, "E97.3.left", {"start": v(-152.95, -36.4) * mm, "end": v(-126.62, -36.4) * mm});
            skLineSegment(sketch, "E97.3.right", {"start": v(-152.95, -46.4) * mm, "end": v(-126.62, -46.4) * mm});
            skArc(sketch, "E97.4.startCap", {"start": v(-113.62, -46.4) * mm, "mid": v(-118.62, -41.4) * mm, "end": v(-113.62, -36.4) * mm});
            skArc(sketch, "E97.4.endCap", {"start": v(-87.29, -36.4) * mm, "mid": v(-82.29, -41.4) * mm, "end": v(-87.29, -46.4) * mm});
            skLineSegment(sketch, "E97.4.left", {"start": v(-113.62, -36.4) * mm, "end": v(-87.29, -36.4) * mm});
            skLineSegment(sketch, "E97.4.right", {"start": v(-113.62, -46.4) * mm, "end": v(-87.29, -46.4) * mm});
            skArc(sketch, "E97.5.startCap", {"start": v(-182.29, -59.52) * mm, "mid": v(-187.29, -54.52) * mm, "end": v(-182.29, -49.52) * mm});
            skArc(sketch, "E97.5.endCap", {"start": v(-146.29, -49.52) * mm, "mid": v(-141.29, -54.52) * mm, "end": v(-146.29, -59.52) * mm});
            skLineSegment(sketch, "E97.5.left", {"start": v(-182.29, -49.52) * mm, "end": v(-146.29, -49.52) * mm});
            skLineSegment(sketch, "E97.5.right", {"start": v(-182.29, -59.52) * mm, "end": v(-146.29, -59.52) * mm});
            skArc(sketch, "E97.6.startCap", {"start": v(-133.29, -59.52) * mm, "mid": v(-138.29, -54.52) * mm, "end": v(-133.29, -49.52) * mm});
            skArc(sketch, "E97.6.endCap", {"start": v(-97.29, -49.52) * mm, "mid": v(-92.29, -54.52) * mm, "end": v(-97.29, -59.52) * mm});
            skLineSegment(sketch, "E97.6.left", {"start": v(-133.29, -49.52) * mm, "end": v(-97.29, -49.52) * mm});
            skLineSegment(sketch, "E97.6.right", {"start": v(-133.29, -59.52) * mm, "end": v(-97.29, -59.52) * mm});
            skCircle(sketch, "E98", {"center": v(-192.29, -54.52) * mm, "radius": 2.5 * mm});
            skCircle(sketch, "E99", {"center": v(-87.29, -54.52) * mm, "radius": 2.5 * mm});
            skSolve(sketch);
        }
        {
            var Q0;
            Q0=qSketchRegion(id+"F15",true);
            var Q1;
            {var subQ0=sQuery(id+"F15.wireOp",EDGE,"eD3hBwOG-1YSv-rIqv-KxOD-YYoGhDVYBiqk");Q1=makeQuery(id+"F15.imprint","IMPRINT",FACE,{"disambiguationData":[TD([[makeQuery(id+"F15.imprint","IMPRINT",EDGE,{"derivedFrom":subQ0}),-1.0]])]});}
            extrude(context, id + "F16", {"entities" : qUnion([Q0, Q1]), "operationType" : NewBodyOperationType.REMOVE, "oppositeDirection" : true, "depth" : 25 * mm});
        }
        {
            var Q0;
            Q0=qCreatedBy(makeId("Top.planeOp"),FACE);
            cPlane(context, id + "F17", {"entities" : qUnion([Q0]), "cplaneType" : CPlaneType.OFFSET, "offset" : 155 * mm, "width" : 150 * mm, "height" : 150 * mm});
        }
        {
            var Q0;
            Q0=qCreatedBy(id+"F17.planeOp",FACE);
            var sketch = newSketch(context, id + "F18", { "sketchPlane" : qUnion([Q0])});
            skLineSegment(sketch, "E100.bottom", {"start": v(-91.02, 152.87) * mm, "end": v(54.98, 152.87) * mm});
            skLineSegment(sketch, "E100.top", {"start": v(-91.02, 65.87) * mm, "end": v(54.98, 65.87) * mm});
            skLineSegment(sketch, "E100.left", {"start": v(-91.02, 152.87) * mm, "end": v(-91.02, 65.87) * mm});
            skLineSegment(sketch, "E100.right", {"start": v(54.98, 152.87) * mm, "end": v(54.98, 65.87) * mm});
            skLineSegment(sketch, "E101", {"start": v(-80.02, 65.87) * mm, "end": v(-83.02, 68.87) * mm});
            skLineSegment(sketch, "E102", {"start": v(43.98, 65.87) * mm, "end": v(46.98, 68.87) * mm});
            skLineSegment(sketch, "E103", {"start": v(-83.02, 68.87) * mm, "end": v(-91.02, 68.87) * mm});
            skLineSegment(sketch, "E104", {"start": v(46.98, 68.87) * mm, "end": v(54.98, 68.87) * mm});
            skLineSegment(sketch, "E105", {"start": v(46.98, 65.87) * mm, "end": v(46.98, 73.87) * mm, "construction": true});
            skCircle(sketch, "E106", {"center": v(46.98, 73.87) * mm, "radius": 1.5 * mm});
            skLineSegment(sketch, "E107", {"start": v(-83.02, 65.87) * mm, "end": v(-83.02, 73.87) * mm, "construction": true});
            skCircle(sketch, "E108", {"center": v(-83.02, 73.87) * mm, "radius": 1.5 * mm});
            skSolve(sketch);
        }
        {
            var Q0;
            {var subQ1=sQuery(id+"F18.wireOp",EDGE,"E100.bottom");Q0=makeQuery(id+"F18.imprint","IMPRINT",FACE,{"disambiguationData":[TD([[makeQuery(id+"F18.imprint","IMPRINT",EDGE,{"derivedFrom":subQ1}),-1.0]])]});}
            extrude(context, id + "F19", {"entities" : qUnion([Q0]), "depth" : 3 * mm});
        }
        {
            var Q0;
            Q0=makeQuery(id+"F19.opExtrude","SWEPT_BODY",BODY,{"disambiguationData":[OSD([sQuery(id+"F18.wireOp",EDGE,"E100.bottom"),sQuery(id+"F18.wireOp",EDGE,"E100.top"),sQuery(id+"F18.wireOp",EDGE,"E100.left"),sQuery(id+"F18.wireOp",EDGE,"E100.right"),sQuery(id+"F18.wireOp",EDGE,"E101"),sQuery(id+"F18.wireOp",EDGE,"3zsQ1Kl9-2ynF-8LIN-0dku-r61PIn4XyDqG"),sQuery(id+"F18.wireOp",EDGE,"UXQkqX4z-jOis-0Iwp-P2ix-A9E3pHhtgsOQ"),sQuery(id+"F18.wireOp",EDGE,"E102"),sQuery(id+"F18.wireOp",EDGE,"LeDl9sKz-5wQR-wnus-53VY-3W6SMz2K6K2i"),sQuery(id+"F18.wireOp",EDGE,"1wH7Y6pB-1Br9-c6Mt-ri01-EdgmEcDOcEDC")])]});
            var Q1;
            Q1=makeQuery(id+"F19.opExtrude","SWEPT_FACE",FACE,{"disambiguationData":[OSD([sQuery(id+"F18.wireOp",EDGE,"E100.bottom")])]});
            mirror(context, id + "F20", {"operationType" : NewBodyOperationType.ADD, "entities" : qUnion([Q0]), "mirrorPlane" : qUnion([Q1])});
        }
        {
            var Q0;
            Q0=qCreatedBy(makeId("Top.planeOp"),FACE);
            cPlane(context, id + "F21", {"entities" : qUnion([Q0]), "cplaneType" : CPlaneType.OFFSET, "offset" : 153 * mm, "oppositeDirection" : true, "width" : 150 * mm, "height" : 150 * mm});
        }
        {
            var Q0;
            Q0=qCreatedBy(id+"F21.planeOp",FACE);
            var sketch = newSketch(context, id + "F22", { "sketchPlane" : qUnion([Q0])});
            skLineSegment(sketch, "E109.bottom", {"start": v(-76.92, 27.42) * mm, "end": v(69.08, 27.42) * mm});
            skLineSegment(sketch, "E109.top", {"start": v(-76.92, 114.42) * mm, "end": v(69.08, 114.42) * mm});
            skLineSegment(sketch, "E109.left", {"start": v(-76.92, 27.42) * mm, "end": v(-76.92, 114.42) * mm});
            skLineSegment(sketch, "E109.right", {"start": v(69.08, 27.42) * mm, "end": v(69.08, 114.42) * mm});
            skLineSegment(sketch, "E110", {"start": v(-65.92, 27.42) * mm, "end": v(-68.92, 30.42) * mm});
            skLineSegment(sketch, "E111", {"start": v(61.08, 30.42) * mm, "end": v(58.08, 27.42) * mm});
            skLineSegment(sketch, "E112", {"start": v(61.08, 30.42) * mm, "end": v(69.08, 30.42) * mm});
            skLineSegment(sketch, "E113", {"start": v(-68.92, 30.42) * mm, "end": v(-76.92, 30.42) * mm});
            skSolve(sketch);
        }
        {
            var Q0;
            {var subQ1=sQuery(id+"F22.wireOp",EDGE,"E109.top");Q0=makeQuery(id+"F22.imprint","IMPRINT",FACE,{"disambiguationData":[TD([[makeQuery(id+"F22.imprint","IMPRINT",EDGE,{"derivedFrom":subQ1}),-1.0]])]});}
            extrude(context, id + "F23", {"entities" : qUnion([Q0]), "depth" : 3 * mm});
        }
        {
            var Q0;
            Q0=makeQuery(id+"F23.opExtrude","SWEPT_BODY",BODY,{"disambiguationData":[OSD([sQuery(id+"F22.wireOp",EDGE,"E109.bottom"),sQuery(id+"F22.wireOp",EDGE,"E109.top"),sQuery(id+"F22.wireOp",EDGE,"E109.left"),sQuery(id+"F22.wireOp",EDGE,"E109.right"),sQuery(id+"F22.wireOp",EDGE,"E110"),sQuery(id+"F22.wireOp",EDGE,"dnEH7a7q-0e2G-ZF1u-gQp3-ZGx2YlrUhsfq"),sQuery(id+"F22.wireOp",EDGE,"EYcrjZ5U-B8Tu-Hvld-BROV-cSRqyUUC4nfP"),sQuery(id+"F22.wireOp",EDGE,"lcQWckg9-mZXk-lsL4-PW7S-RH1iYC4EfrxX"),sQuery(id+"F22.wireOp",EDGE,"m4YSihPu-nfU7-MdAm-Gg2Q-VAeN7eaJ9XWN"),sQuery(id+"F22.wireOp",EDGE,"E111")])]});
            var Q1;
            Q1=makeQuery(id+"F23.opExtrude","SWEPT_FACE",FACE,{"disambiguationData":[OSD([sQuery(id+"F22.wireOp",EDGE,"E109.top")])]});
            mirror(context, id + "F24", {"operationType" : NewBodyOperationType.ADD, "entities" : qUnion([Q0]), "mirrorPlane" : qUnion([Q1])});
        }
        {
            var Q0;
            Q0=qCreatedBy(makeId("Front.planeOp"),FACE);
            cPlane(context, id + "F25", {"entities" : qUnion([Q0]), "cplaneType" : CPlaneType.OFFSET, "offset" : 376 * mm, "oppositeDirection" : true, "width" : 150 * mm, "height" : 150 * mm});
        }
        {
            var Q0;
            {var subQ0=makeQuery(id+"F23.opExtrude","CAP_FACE",FACE,{"disambiguationData":[OSD([sQuery(id+"F22.wireOp",EDGE,"E109.bottom"),sQuery(id+"F22.wireOp",EDGE,"E109.top"),sQuery(id+"F22.wireOp",EDGE,"E109.left"),sQuery(id+"F22.wireOp",EDGE,"E109.right"),sQuery(id+"F22.wireOp",EDGE,"E110"),sQuery(id+"F22.wireOp",EDGE,"dnEH7a7q-0e2G-ZF1u-gQp3-ZGx2YlrUhsfq"),sQuery(id+"F22.wireOp",EDGE,"EYcrjZ5U-B8Tu-Hvld-BROV-cSRqyUUC4nfP"),sQuery(id+"F22.wireOp",EDGE,"lcQWckg9-mZXk-lsL4-PW7S-RH1iYC4EfrxX"),sQuery(id+"F22.wireOp",EDGE,"m4YSihPu-nfU7-MdAm-Gg2Q-VAeN7eaJ9XWN"),sQuery(id+"F22.wireOp",EDGE,"E111")])],"isStart":true});Q0=makeQuery(id+"F24.boolean.opBoolean","MERGE",FACE,{"derivedFrom":[subQ0,makeQuery(id+"F24.opPattern","COPY",FACE,{"derivedFrom":subQ0,"instanceName":"1"})]});}
            var sketch = newSketch(context, id + "F26", { "sketchPlane" : qUnion([Q0])});
            skLineSegment(sketch, "E114", {"start": v(-53.42, -177.42) * mm, "end": v(-53.42, -155.42) * mm, "construction": true});
            skLineSegment(sketch, "E115", {"start": v(-53.42, -155.42) * mm, "end": v(-53.42, -142.76) * mm, "construction": true});
            skLineSegment(sketch, "E116", {"start": v(-53.42, -142.76) * mm, "end": v(-53.42, -120.76) * mm, "construction": true});
            skLineSegment(sketch, "E117", {"start": v(-53.42, -120.76) * mm, "end": v(-53.42, -108.1) * mm, "construction": true});
            skLineSegment(sketch, "E118", {"start": v(-53.42, -108.1) * mm, "end": v(-53.42, -86.1) * mm, "construction": true});
            skLineSegment(sketch, "E119", {"start": v(-53.42, -86.1) * mm, "end": v(-53.42, -73.42) * mm, "construction": true});
            skLineSegment(sketch, "E120", {"start": v(-53.42, -177.42) * mm, "end": v(-53.42, -201.42) * mm, "construction": true});
            skLineSegment(sketch, "E121", {"start": v(-53.42, -73.42) * mm, "end": v(-53.42, -51.42) * mm, "construction": true});
            skLineSegment(sketch, "E122", {"start": v(-53.42, -51.42) * mm, "end": v(-53.42, -27.42) * mm, "construction": true});
            skArc(sketch, "E123.0.startCap", {"start": v(-48.42, -177.42) * mm, "mid": v(-53.42, -182.42) * mm, "end": v(-58.42, -177.42) * mm});
            skArc(sketch, "E123.0.endCap", {"start": v(-58.42, -155.42) * mm, "mid": v(-53.42, -150.42) * mm, "end": v(-48.42, -155.42) * mm});
            skLineSegment(sketch, "E123.0.left", {"start": v(-58.42, -177.42) * mm, "end": v(-58.42, -155.42) * mm});
            skLineSegment(sketch, "E123.0.right", {"start": v(-48.42, -177.42) * mm, "end": v(-48.42, -155.42) * mm});
            skArc(sketch, "E123.1.startCap", {"start": v(-48.42, -142.76) * mm, "mid": v(-53.42, -147.76) * mm, "end": v(-58.42, -142.76) * mm});
            skArc(sketch, "E123.1.endCap", {"start": v(-58.42, -120.76) * mm, "mid": v(-53.42, -115.76) * mm, "end": v(-48.42, -120.76) * mm});
            skLineSegment(sketch, "E123.1.left", {"start": v(-58.42, -142.76) * mm, "end": v(-58.42, -120.76) * mm});
            skLineSegment(sketch, "E123.1.right", {"start": v(-48.42, -142.76) * mm, "end": v(-48.42, -120.76) * mm});
            skArc(sketch, "E123.2.startCap", {"start": v(-48.42, -108.1) * mm, "mid": v(-53.42, -113.1) * mm, "end": v(-58.42, -108.1) * mm});
            skArc(sketch, "E123.2.endCap", {"start": v(-58.42, -86.1) * mm, "mid": v(-53.42, -81.1) * mm, "end": v(-48.42, -86.1) * mm});
            skLineSegment(sketch, "E123.2.left", {"start": v(-58.42, -108.1) * mm, "end": v(-58.42, -86.1) * mm});
            skLineSegment(sketch, "E123.2.right", {"start": v(-48.42, -108.1) * mm, "end": v(-48.42, -86.1) * mm});
            skArc(sketch, "E123.3.startCap", {"start": v(-48.42, -73.42) * mm, "mid": v(-53.42, -78.42) * mm, "end": v(-58.42, -73.42) * mm});
            skArc(sketch, "E123.3.endCap", {"start": v(-58.42, -51.42) * mm, "mid": v(-53.42, -46.42) * mm, "end": v(-48.42, -51.42) * mm});
            skLineSegment(sketch, "E123.3.left", {"start": v(-58.42, -73.42) * mm, "end": v(-58.42, -51.42) * mm});
            skLineSegment(sketch, "E123.3.right", {"start": v(-48.42, -73.42) * mm, "end": v(-48.42, -51.42) * mm});
            skArc(sketch, "E124.1.0.0", {"start": v(-30.42, -177.42) * mm, "mid": v(-35.42, -182.42) * mm, "end": v(-40.42, -177.42) * mm});
            skLineSegment(sketch, "E124.1.0.1", {"start": v(-30.42, -177.42) * mm, "end": v(-30.42, -155.42) * mm});
            skLineSegment(sketch, "E124.1.0.2", {"start": v(-40.42, -177.42) * mm, "end": v(-40.42, -155.42) * mm});
            skArc(sketch, "E124.1.0.3", {"start": v(-40.42, -155.42) * mm, "mid": v(-35.42, -150.42) * mm, "end": v(-30.42, -155.42) * mm});
            skArc(sketch, "E124.1.0.4", {"start": v(-30.42, -142.76) * mm, "mid": v(-35.42, -147.76) * mm, "end": v(-40.42, -142.76) * mm});
            skLineSegment(sketch, "E124.1.0.5", {"start": v(-30.42, -142.76) * mm, "end": v(-30.42, -120.76) * mm});
            skLineSegment(sketch, "E124.1.0.6", {"start": v(-40.42, -142.76) * mm, "end": v(-40.42, -120.76) * mm});
            skArc(sketch, "E124.1.0.7", {"start": v(-40.42, -120.76) * mm, "mid": v(-35.42, -115.76) * mm, "end": v(-30.42, -120.76) * mm});
            skLineSegment(sketch, "E124.1.0.8", {"start": v(-30.42, -108.1) * mm, "end": v(-30.42, -86.1) * mm});
            skArc(sketch, "E124.1.0.9", {"start": v(-30.42, -108.1) * mm, "mid": v(-35.42, -113.1) * mm, "end": v(-40.42, -108.1) * mm});
            skLineSegment(sketch, "E124.1.0.10", {"start": v(-40.42, -108.1) * mm, "end": v(-40.42, -86.1) * mm});
            skArc(sketch, "E124.1.0.11", {"start": v(-40.42, -86.1) * mm, "mid": v(-35.42, -81.1) * mm, "end": v(-30.42, -86.1) * mm});
            skArc(sketch, "E124.1.0.12", {"start": v(-30.42, -73.42) * mm, "mid": v(-35.42, -78.42) * mm, "end": v(-40.42, -73.42) * mm});
            skLineSegment(sketch, "E124.1.0.13", {"start": v(-30.42, -73.42) * mm, "end": v(-30.42, -51.42) * mm});
            skLineSegment(sketch, "E124.1.0.14", {"start": v(-40.42, -73.42) * mm, "end": v(-40.42, -51.42) * mm});
            skArc(sketch, "E124.1.0.15", {"start": v(-40.42, -51.42) * mm, "mid": v(-35.42, -46.42) * mm, "end": v(-30.42, -51.42) * mm});
            skArc(sketch, "E124.2.0.0", {"start": v(-12.42, -177.42) * mm, "mid": v(-17.42, -182.42) * mm, "end": v(-22.42, -177.42) * mm});
            skLineSegment(sketch, "E124.2.0.1", {"start": v(-12.42, -177.42) * mm, "end": v(-12.42, -155.42) * mm});
            skLineSegment(sketch, "E124.2.0.2", {"start": v(-22.42, -177.42) * mm, "end": v(-22.42, -155.42) * mm});
            skArc(sketch, "E124.2.0.3", {"start": v(-22.42, -155.42) * mm, "mid": v(-17.42, -150.42) * mm, "end": v(-12.42, -155.42) * mm});
            skArc(sketch, "E124.2.0.4", {"start": v(-12.42, -142.76) * mm, "mid": v(-17.42, -147.76) * mm, "end": v(-22.42, -142.76) * mm});
            skLineSegment(sketch, "E124.2.0.5", {"start": v(-12.42, -142.76) * mm, "end": v(-12.42, -120.76) * mm});
            skLineSegment(sketch, "E124.2.0.6", {"start": v(-22.42, -142.76) * mm, "end": v(-22.42, -120.76) * mm});
            skArc(sketch, "E124.2.0.7", {"start": v(-22.42, -120.76) * mm, "mid": v(-17.42, -115.76) * mm, "end": v(-12.42, -120.76) * mm});
            skLineSegment(sketch, "E124.2.0.8", {"start": v(-12.42, -108.1) * mm, "end": v(-12.42, -86.1) * mm});
            skArc(sketch, "E124.2.0.9", {"start": v(-12.42, -108.1) * mm, "mid": v(-17.42, -113.1) * mm, "end": v(-22.42, -108.1) * mm});
            skLineSegment(sketch, "E124.2.0.10", {"start": v(-22.42, -108.1) * mm, "end": v(-22.42, -86.1) * mm});
            skArc(sketch, "E124.2.0.11", {"start": v(-22.42, -86.1) * mm, "mid": v(-17.42, -81.1) * mm, "end": v(-12.42, -86.1) * mm});
            skArc(sketch, "E124.2.0.12", {"start": v(-12.42, -73.42) * mm, "mid": v(-17.42, -78.42) * mm, "end": v(-22.42, -73.42) * mm});
            skLineSegment(sketch, "E124.2.0.13", {"start": v(-12.42, -73.42) * mm, "end": v(-12.42, -51.42) * mm});
            skLineSegment(sketch, "E124.2.0.14", {"start": v(-22.42, -73.42) * mm, "end": v(-22.42, -51.42) * mm});
            skArc(sketch, "E124.2.0.15", {"start": v(-22.42, -51.42) * mm, "mid": v(-17.42, -46.42) * mm, "end": v(-12.42, -51.42) * mm});
            skArc(sketch, "E124.3.0.0", {"start": v(5.58, -177.42) * mm, "mid": v(0.58, -182.42) * mm, "end": v(-4.42, -177.42) * mm});
            skLineSegment(sketch, "E124.3.0.1", {"start": v(5.58, -177.42) * mm, "end": v(5.58, -155.42) * mm});
            skLineSegment(sketch, "E124.3.0.2", {"start": v(-4.42, -177.42) * mm, "end": v(-4.42, -155.42) * mm});
            skArc(sketch, "E124.3.0.3", {"start": v(-4.42, -155.42) * mm, "mid": v(0.58, -150.42) * mm, "end": v(5.58, -155.42) * mm});
            skArc(sketch, "E124.3.0.4", {"start": v(5.58, -142.76) * mm, "mid": v(0.58, -147.76) * mm, "end": v(-4.42, -142.76) * mm});
            skLineSegment(sketch, "E124.3.0.5", {"start": v(5.58, -142.76) * mm, "end": v(5.58, -120.76) * mm});
            skLineSegment(sketch, "E124.3.0.6", {"start": v(-4.42, -142.76) * mm, "end": v(-4.42, -120.76) * mm});
            skArc(sketch, "E124.3.0.7", {"start": v(-4.42, -120.76) * mm, "mid": v(0.58, -115.76) * mm, "end": v(5.58, -120.76) * mm});
            skLineSegment(sketch, "E124.3.0.8", {"start": v(5.58, -108.1) * mm, "end": v(5.58, -86.1) * mm});
            skArc(sketch, "E124.3.0.9", {"start": v(5.58, -108.1) * mm, "mid": v(0.58, -113.1) * mm, "end": v(-4.42, -108.1) * mm});
            skLineSegment(sketch, "E124.3.0.10", {"start": v(-4.42, -108.1) * mm, "end": v(-4.42, -86.1) * mm});
            skArc(sketch, "E124.3.0.11", {"start": v(-4.42, -86.1) * mm, "mid": v(0.58, -81.1) * mm, "end": v(5.58, -86.1) * mm});
            skArc(sketch, "E124.3.0.12", {"start": v(5.58, -73.42) * mm, "mid": v(0.58, -78.42) * mm, "end": v(-4.42, -73.42) * mm});
            skLineSegment(sketch, "E124.3.0.13", {"start": v(5.58, -73.42) * mm, "end": v(5.58, -51.42) * mm});
            skLineSegment(sketch, "E124.3.0.14", {"start": v(-4.42, -73.42) * mm, "end": v(-4.42, -51.42) * mm});
            skArc(sketch, "E124.3.0.15", {"start": v(-4.42, -51.42) * mm, "mid": v(0.58, -46.42) * mm, "end": v(5.58, -51.42) * mm});
            skArc(sketch, "E124.4.0.0", {"start": v(23.58, -177.42) * mm, "mid": v(18.58, -182.42) * mm, "end": v(13.58, -177.42) * mm});
            skLineSegment(sketch, "E124.4.0.1", {"start": v(23.58, -177.42) * mm, "end": v(23.58, -155.42) * mm});
            skLineSegment(sketch, "E124.4.0.2", {"start": v(13.58, -177.42) * mm, "end": v(13.58, -155.42) * mm});
            skArc(sketch, "E124.4.0.3", {"start": v(13.58, -155.42) * mm, "mid": v(18.58, -150.42) * mm, "end": v(23.58, -155.42) * mm});
            skArc(sketch, "E124.4.0.4", {"start": v(23.58, -142.76) * mm, "mid": v(18.58, -147.76) * mm, "end": v(13.58, -142.76) * mm});
            skLineSegment(sketch, "E124.4.0.5", {"start": v(23.58, -142.76) * mm, "end": v(23.58, -120.76) * mm});
            skLineSegment(sketch, "E124.4.0.6", {"start": v(13.58, -142.76) * mm, "end": v(13.58, -120.76) * mm});
            skArc(sketch, "E124.4.0.7", {"start": v(13.58, -120.76) * mm, "mid": v(18.58, -115.76) * mm, "end": v(23.58, -120.76) * mm});
            skLineSegment(sketch, "E124.4.0.8", {"start": v(23.58, -108.1) * mm, "end": v(23.58, -86.1) * mm});
            skArc(sketch, "E124.4.0.9", {"start": v(23.58, -108.1) * mm, "mid": v(18.58, -113.1) * mm, "end": v(13.58, -108.1) * mm});
            skLineSegment(sketch, "E124.4.0.10", {"start": v(13.58, -108.1) * mm, "end": v(13.58, -86.1) * mm});
            skArc(sketch, "E124.4.0.11", {"start": v(13.58, -86.1) * mm, "mid": v(18.58, -81.1) * mm, "end": v(23.58, -86.1) * mm});
            skArc(sketch, "E124.4.0.12", {"start": v(23.58, -73.42) * mm, "mid": v(18.58, -78.42) * mm, "end": v(13.58, -73.42) * mm});
            skLineSegment(sketch, "E124.4.0.13", {"start": v(23.58, -73.42) * mm, "end": v(23.58, -51.42) * mm});
            skLineSegment(sketch, "E124.4.0.14", {"start": v(13.58, -73.42) * mm, "end": v(13.58, -51.42) * mm});
            skArc(sketch, "E124.4.0.15", {"start": v(13.58, -51.42) * mm, "mid": v(18.58, -46.42) * mm, "end": v(23.58, -51.42) * mm});
            skArc(sketch, "E124.5.0.0", {"start": v(41.58, -177.42) * mm, "mid": v(36.58, -182.42) * mm, "end": v(31.58, -177.42) * mm});
            skLineSegment(sketch, "E124.5.0.1", {"start": v(41.58, -177.42) * mm, "end": v(41.58, -155.42) * mm});
            skLineSegment(sketch, "E124.5.0.2", {"start": v(31.58, -177.42) * mm, "end": v(31.58, -155.42) * mm});
            skArc(sketch, "E124.5.0.3", {"start": v(31.58, -155.42) * mm, "mid": v(36.58, -150.42) * mm, "end": v(41.58, -155.42) * mm});
            skArc(sketch, "E124.5.0.4", {"start": v(41.58, -142.76) * mm, "mid": v(36.58, -147.76) * mm, "end": v(31.58, -142.76) * mm});
            skLineSegment(sketch, "E124.5.0.5", {"start": v(41.58, -142.76) * mm, "end": v(41.58, -120.76) * mm});
            skLineSegment(sketch, "E124.5.0.6", {"start": v(31.58, -142.76) * mm, "end": v(31.58, -120.76) * mm});
            skArc(sketch, "E124.5.0.7", {"start": v(31.58, -120.76) * mm, "mid": v(36.58, -115.76) * mm, "end": v(41.58, -120.76) * mm});
            skLineSegment(sketch, "E124.5.0.8", {"start": v(41.58, -108.1) * mm, "end": v(41.58, -86.1) * mm});
            skArc(sketch, "E124.5.0.9", {"start": v(41.58, -108.1) * mm, "mid": v(36.58, -113.1) * mm, "end": v(31.58, -108.1) * mm});
            skLineSegment(sketch, "E124.5.0.10", {"start": v(31.58, -108.1) * mm, "end": v(31.58, -86.1) * mm});
            skArc(sketch, "E124.5.0.11", {"start": v(31.58, -86.1) * mm, "mid": v(36.58, -81.1) * mm, "end": v(41.58, -86.1) * mm});
            skArc(sketch, "E124.5.0.12", {"start": v(41.58, -73.42) * mm, "mid": v(36.58, -78.42) * mm, "end": v(31.58, -73.42) * mm});
            skLineSegment(sketch, "E124.5.0.13", {"start": v(41.58, -73.42) * mm, "end": v(41.58, -51.42) * mm});
            skLineSegment(sketch, "E124.5.0.14", {"start": v(31.58, -73.42) * mm, "end": v(31.58, -51.42) * mm});
            skArc(sketch, "E124.5.0.15", {"start": v(31.58, -51.42) * mm, "mid": v(36.58, -46.42) * mm, "end": v(41.58, -51.42) * mm});
            skLineSegment(sketch, "E124.direction1", {"start": v(-58.42, -177.42) * mm, "end": v(-40.42, -177.42) * mm, "construction": true});
            skSolve(sketch);
        }
        {
            var Q0;
            Q0=qSketchRegion(id+"F26",true);
            extrude(context, id + "F27", {"entities" : qUnion([Q0]), "operationType" : NewBodyOperationType.REMOVE, "oppositeDirection" : true, "depth" : 25 * mm});
        }
        {
            var Q0;
            Q0=qCreatedBy(id+"F25.planeOp",FACE);
            var sketch = newSketch(context, id + "F28", { "sketchPlane" : qUnion([Q0])});
            skLineSegment(sketch, "E125.bottom", {"start": v(-66, 121) * mm, "end": v(80, 121) * mm});
            skLineSegment(sketch, "E125.top", {"start": v(-66, 8.5) * mm, "end": v(80, 8.5) * mm});
            skLineSegment(sketch, "E125.left", {"start": v(-66, 121) * mm, "end": v(-66, 8.5) * mm});
            skLineSegment(sketch, "E125.right", {"start": v(80, 121) * mm, "end": v(80, 8.5) * mm});
            skLineSegment(sketch, "E126", {"start": v(-64, 113.5) * mm, "end": v(-58.5, 119) * mm});
            skLineSegment(sketch, "E127", {"start": v(72, 121) * mm, "end": v(72, 113) * mm, "construction": true});
            skCircle(sketch, "E128", {"center": v(72, 113) * mm, "radius": 1.5 * mm});
            skLineSegment(sketch, "E129", {"start": v(-58, 121) * mm, "end": v(-58, 113) * mm, "construction": true});
            skCircle(sketch, "E130", {"center": v(-58, 113) * mm, "radius": 1.5 * mm});
            skLineSegment(sketch, "E131", {"start": v(78, 113.5) * mm, "end": v(72.5, 119) * mm});
            skLineSegment(sketch, "E132", {"start": v(72.5, 119) * mm, "end": v(-58.5, 119) * mm});
            skLineSegment(sketch, "E133", {"start": v(78, 113.5) * mm, "end": v(78, 110) * mm});
            skLineSegment(sketch, "E134", {"start": v(78, 110) * mm, "end": v(80, 110) * mm});
            skLineSegment(sketch, "E135", {"start": v(-64, 113.5) * mm, "end": v(-64, 110) * mm});
            skLineSegment(sketch, "E136", {"start": v(-64, 110) * mm, "end": v(-66, 110) * mm});
            skSolve(sketch);
        }
        {
            var Q0;
            {var subQ1=sQuery(id+"F28.wireOp",EDGE,"E125.top");Q0=makeQuery(id+"F28.imprint","IMPRINT",FACE,{"disambiguationData":[TD([[makeQuery(id+"F28.imprint","IMPRINT",EDGE,{"derivedFrom":subQ1}),1.0]])]});}
            extrude(context, id + "F29", {"entities" : qUnion([Q0]), "depth" : 3 * mm});
        }
        {
            var Q0;
            Q0=makeQuery(id+"F29.opExtrude","SWEPT_BODY",BODY,{"disambiguationData":[OSD([sQuery(id+"F28.wireOp",EDGE,"E125.bottom"),sQuery(id+"F28.wireOp",EDGE,"E125.top"),sQuery(id+"F28.wireOp",EDGE,"E125.left"),sQuery(id+"F28.wireOp",EDGE,"E125.right"),sQuery(id+"F28.wireOp",EDGE,"88c43418-5c0f-4f09-8127-112137b7eb87"),sQuery(id+"F28.wireOp",EDGE,"E126"),sQuery(id+"F28.wireOp",EDGE,"ccf2e9e3-9b64-4f2a-9f18-310bc790516a"),sQuery(id+"F28.wireOp",EDGE,"c5f426b9-73f2-4868-9408-4cfd947a191f"),sQuery(id+"F28.wireOp",EDGE,"cd8d91dd-9a42-4ae4-8430-5a7eccad3886"),sQuery(id+"F28.wireOp",EDGE,"f1dcae7c-8bd8-43e5-b7b1-ff3532f110ef")])]});
            var Q1;
            Q1=makeQuery(id+"F29.opExtrude","SWEPT_FACE",FACE,{"disambiguationData":[OSD([sQuery(id+"F28.wireOp",EDGE,"E125.top")])]});
            mirror(context, id + "F30", {"operationType" : NewBodyOperationType.ADD, "entities" : qUnion([Q0]), "mirrorPlane" : qUnion([Q1])});
        }
        {
            var Q0;
            {var subQ0=makeQuery(id+"F29.opExtrude","CAP_FACE",FACE,{"disambiguationData":[OSD([sQuery(id+"F28.wireOp",EDGE,"E125.bottom"),sQuery(id+"F28.wireOp",EDGE,"E125.top"),sQuery(id+"F28.wireOp",EDGE,"E125.left"),sQuery(id+"F28.wireOp",EDGE,"E125.right"),sQuery(id+"F28.wireOp",EDGE,"88c43418-5c0f-4f09-8127-112137b7eb87"),sQuery(id+"F28.wireOp",EDGE,"E126"),sQuery(id+"F28.wireOp",EDGE,"ccf2e9e3-9b64-4f2a-9f18-310bc790516a"),sQuery(id+"F28.wireOp",EDGE,"c5f426b9-73f2-4868-9408-4cfd947a191f"),sQuery(id+"F28.wireOp",EDGE,"cd8d91dd-9a42-4ae4-8430-5a7eccad3886"),sQuery(id+"F28.wireOp",EDGE,"f1dcae7c-8bd8-43e5-b7b1-ff3532f110ef")])],"isStart":true});Q0=makeQuery(id+"F30.boolean.opBoolean","MERGE",FACE,{"derivedFrom":[subQ0,makeQuery(id+"F30.opPattern","COPY",FACE,{"derivedFrom":subQ0,"instanceName":"1"})]});}
            var sketch = newSketch(context, id + "F31", { "sketchPlane" : qUnion([Q0])});
            skLineSegment(sketch, "E137", {"start": v(-72, 103) * mm, "end": v(-72, -67) * mm, "construction": true});
            skLineSegment(sketch, "E138", {"start": v(-72, -67) * mm, "end": v(-80, -67) * mm, "construction": true});
            skLineSegment(sketch, "E139", {"start": v(-72, -65.7) * mm, "end": v(-63.9, -65.7) * mm, "construction": true});
            skLineSegment(sketch, "E140.bottom", {"start": v(-63.9, -73.65) * mm, "end": v(33.1, -73.65) * mm});
            skLineSegment(sketch, "E140.top", {"start": v(-63.9, -57.75) * mm, "end": v(33.1, -57.75) * mm});
            skLineSegment(sketch, "E140.left", {"start": v(-63.9, -73.65) * mm, "end": v(-63.9, -57.75) * mm});
            skLineSegment(sketch, "E140.right", {"start": v(33.1, -73.65) * mm, "end": v(33.1, -57.75) * mm});
            skLineSegment(sketch, "E141.bottom", {"start": v(-63.9, -78.05) * mm, "end": v(33.1, -78.05) * mm});
            skLineSegment(sketch, "E141.top", {"start": v(-63.9, -93.95) * mm, "end": v(33.1, -93.95) * mm});
            skLineSegment(sketch, "E141.left", {"start": v(-63.9, -78.05) * mm, "end": v(-63.9, -93.95) * mm});
            skLineSegment(sketch, "E141.right", {"start": v(33.1, -78.05) * mm, "end": v(33.1, -93.95) * mm});
            skLineSegment(sketch, "E142", {"start": v(33.1, -78.05) * mm, "end": v(33.1, -73.65) * mm, "construction": true});
            skLineSegment(sketch, "E143.bottom", {"start": v(-29.6, 105.6) * mm, "end": v(-74.3, 105.6) * mm});
            skLineSegment(sketch, "E144", {"start": v(-74.3, 105.6) * mm, "end": v(-74.3, -53.4) * mm});
            skLineSegment(sketch, "E145", {"start": v(-74.3, -53.4) * mm, "end": v(-29.6, -53.4) * mm});
            skLineSegment(sketch, "E146", {"start": v(-29.6, -53.4) * mm, "end": v(-29.6, 105.6) * mm});
            skArc(sketch, "E147", {"start": v(-73.55, 105.6) * mm, "mid": v(-74.83, 106.13) * mm, "end": v(-74.3, 104.85) * mm});
            skArc(sketch, "E148", {"start": v(-29.6, 104.85) * mm, "mid": v(-29.07, 106.13) * mm, "end": v(-30.35, 105.6) * mm});
            skArc(sketch, "E149", {"start": v(-30.35, -53.32) * mm, "mid": v(-29.1, -53.96) * mm, "end": v(-29.6, -52.65) * mm});
            skArc(sketch, "E150", {"start": v(-74.3, -52.65) * mm, "mid": v(-74.83, -53.93) * mm, "end": v(-73.55, -53.4) * mm});
            skLineSegment(sketch, "E151", {"start": v(37.5, -53.25) * mm, "end": v(37.5, -93.25) * mm});
            skLineSegment(sketch, "E152", {"start": v(33.1, -57.75) * mm, "end": v(37.5, -57.75) * mm, "construction": true});
            skLineSegment(sketch, "E153", {"start": v(37.5, -93.25) * mm, "end": v(45.5, -93.25) * mm});
            skLineSegment(sketch, "E154", {"start": v(45.5, -93.25) * mm, "end": v(53.5, -85.25) * mm});
            skLineSegment(sketch, "E155", {"start": v(53.5, -85.25) * mm, "end": v(53.5, -43.25) * mm});
            skLineSegment(sketch, "E156", {"start": v(37.5, -53.25) * mm, "end": v(40.5, -53.25) * mm});
            skLineSegment(sketch, "E157", {"start": v(40.5, -53.25) * mm, "end": v(50.5, -43.25) * mm});
            skLineSegment(sketch, "E158", {"start": v(50.5, -43.25) * mm, "end": v(53.5, -43.25) * mm});
            skLineSegment(sketch, "E159", {"start": v(-72.5, -102) * mm, "end": v(-80, -102) * mm, "construction": true});
            skSolve(sketch);
        }
        {
            var Q0;
            {var subQ0=makeQuery(id+"F29.opExtrude","CAP_FACE",FACE,{"disambiguationData":[OSD([sQuery(id+"F28.wireOp",EDGE,"E125.bottom"),sQuery(id+"F28.wireOp",EDGE,"E125.top"),sQuery(id+"F28.wireOp",EDGE,"E125.left"),sQuery(id+"F28.wireOp",EDGE,"E125.right"),sQuery(id+"F28.wireOp",EDGE,"88c43418-5c0f-4f09-8127-112137b7eb87"),sQuery(id+"F28.wireOp",EDGE,"E126"),sQuery(id+"F28.wireOp",EDGE,"ccf2e9e3-9b64-4f2a-9f18-310bc790516a"),sQuery(id+"F28.wireOp",EDGE,"c5f426b9-73f2-4868-9408-4cfd947a191f"),sQuery(id+"F28.wireOp",EDGE,"cd8d91dd-9a42-4ae4-8430-5a7eccad3886"),sQuery(id+"F28.wireOp",EDGE,"f1dcae7c-8bd8-43e5-b7b1-ff3532f110ef")])],"isStart":true});Q0=makeQuery(id+"F30.boolean.opBoolean","MERGE",FACE,{"derivedFrom":[subQ0,makeQuery(id+"F30.opPattern","COPY",FACE,{"derivedFrom":subQ0,"instanceName":"1"})]});}
            var sketch = newSketch(context, id + "F32", { "sketchPlane" : qUnion([Q0])});
            skLineSegment(sketch, "E160", {"start": v(-3.25, 65.5) * mm, "end": v(-3.25, 41.5) * mm, "construction": true});
            skLineSegment(sketch, "E161", {"start": v(-3.25, 41.5) * mm, "end": v(-3.25, 27.5) * mm, "construction": true});
            skLineSegment(sketch, "E162", {"start": v(-3.25, 27.5) * mm, "end": v(-3.25, 3.5) * mm, "construction": true});
            skLineSegment(sketch, "E163", {"start": v(-3.25, 3.5) * mm, "end": v(-3.25, -10.5) * mm, "construction": true});
            skLineSegment(sketch, "E164", {"start": v(-3.25, -10.5) * mm, "end": v(-3.25, -34.5) * mm, "construction": true});
            skArc(sketch, "E165.0.startCap", {"start": v(-7.25, 65.5) * mm, "mid": v(-3.25, 69.5) * mm, "end": v(0.75, 65.5) * mm});
            skArc(sketch, "E165.0.endCap", {"start": v(0.75, 41.5) * mm, "mid": v(-3.25, 37.5) * mm, "end": v(-7.25, 41.5) * mm});
            skLineSegment(sketch, "E165.0.left", {"start": v(0.75, 65.5) * mm, "end": v(0.75, 41.5) * mm});
            skLineSegment(sketch, "E165.0.right", {"start": v(-7.25, 65.5) * mm, "end": v(-7.25, 41.5) * mm});
            skArc(sketch, "E165.1.startCap", {"start": v(-7.25, 27.5) * mm, "mid": v(-3.25, 31.5) * mm, "end": v(0.75, 27.5) * mm});
            skArc(sketch, "E165.1.endCap", {"start": v(0.75, 3.5) * mm, "mid": v(-3.25, -0.5) * mm, "end": v(-7.25, 3.5) * mm});
            skLineSegment(sketch, "E165.1.left", {"start": v(0.75, 27.5) * mm, "end": v(0.75, 3.5) * mm});
            skLineSegment(sketch, "E165.1.right", {"start": v(-7.25, 27.5) * mm, "end": v(-7.25, 3.5) * mm});
            skArc(sketch, "E165.2.startCap", {"start": v(-7.25, -10.5) * mm, "mid": v(-3.25, -6.5) * mm, "end": v(0.75, -10.5) * mm});
            skArc(sketch, "E165.2.endCap", {"start": v(0.75, -34.5) * mm, "mid": v(-3.25, -38.5) * mm, "end": v(-7.25, -34.5) * mm});
            skLineSegment(sketch, "E165.2.left", {"start": v(0.75, -10.5) * mm, "end": v(0.75, -34.5) * mm});
            skLineSegment(sketch, "E165.2.right", {"start": v(-7.25, -10.5) * mm, "end": v(-7.25, -34.5) * mm});
            skLineSegment(sketch, "E166.1.0.0", {"start": v(10.75, 27.5) * mm, "end": v(10.75, 3.5) * mm});
            skArc(sketch, "E166.1.0.1", {"start": v(10.75, -10.5) * mm, "mid": v(14.75, -6.5) * mm, "end": v(18.75, -10.5) * mm});
            skArc(sketch, "E166.1.0.3", {"start": v(10.75, 65.5) * mm, "mid": v(14.75, 69.5) * mm, "end": v(18.75, 65.5) * mm});
            skLineSegment(sketch, "E166.1.0.4", {"start": v(10.75, -10.5) * mm, "end": v(10.75, -34.5) * mm});
            skArc(sketch, "E166.1.0.5", {"start": v(10.75, 27.5) * mm, "mid": v(14.75, 31.5) * mm, "end": v(18.75, 27.5) * mm});
            skArc(sketch, "E166.1.0.6", {"start": v(18.75, -34.5) * mm, "mid": v(14.75, -38.5) * mm, "end": v(10.75, -34.5) * mm});
            skArc(sketch, "E166.1.0.7", {"start": v(18.75, 3.5) * mm, "mid": v(14.75, -0.5) * mm, "end": v(10.75, 3.5) * mm});
            skLineSegment(sketch, "E166.1.0.11", {"start": v(14.75, -10.5) * mm, "end": v(14.75, -34.5) * mm, "construction": true});
            skLineSegment(sketch, "E166.1.0.12", {"start": v(14.75, 3.5) * mm, "end": v(14.75, -10.5) * mm, "construction": true});
            skLineSegment(sketch, "E166.1.0.13", {"start": v(14.75, 27.5) * mm, "end": v(14.75, 3.5) * mm, "construction": true});
            skLineSegment(sketch, "E166.1.0.14", {"start": v(14.75, 41.5) * mm, "end": v(14.75, 27.5) * mm, "construction": true});
            skLineSegment(sketch, "E166.1.0.15", {"start": v(14.75, 65.5) * mm, "end": v(14.75, 41.5) * mm, "construction": true});
            skLineSegment(sketch, "E166.1.0.16", {"start": v(18.75, 27.5) * mm, "end": v(18.75, 3.5) * mm});
            skLineSegment(sketch, "E166.1.0.20", {"start": v(10.75, 65.5) * mm, "end": v(10.75, 41.5) * mm});
            skLineSegment(sketch, "E166.1.0.21", {"start": v(18.75, 65.5) * mm, "end": v(18.75, 41.5) * mm});
            skArc(sketch, "E166.1.0.22", {"start": v(18.75, 41.5) * mm, "mid": v(14.75, 37.5) * mm, "end": v(10.75, 41.5) * mm});
            skLineSegment(sketch, "E166.1.0.23", {"start": v(18.75, -10.5) * mm, "end": v(18.75, -34.5) * mm});
            skLineSegment(sketch, "E166.2.0.0", {"start": v(28.75, 27.5) * mm, "end": v(28.75, 3.5) * mm});
            skArc(sketch, "E166.2.0.1", {"start": v(28.75, -10.5) * mm, "mid": v(32.75, -6.5) * mm, "end": v(36.75, -10.5) * mm});
            skArc(sketch, "E166.2.0.3", {"start": v(28.75, 65.5) * mm, "mid": v(32.75, 69.5) * mm, "end": v(36.75, 65.5) * mm});
            skLineSegment(sketch, "E166.2.0.4", {"start": v(28.75, -10.5) * mm, "end": v(28.75, -34.5) * mm});
            skArc(sketch, "E166.2.0.5", {"start": v(28.75, 27.5) * mm, "mid": v(32.75, 31.5) * mm, "end": v(36.75, 27.5) * mm});
            skArc(sketch, "E166.2.0.6", {"start": v(36.75, -34.5) * mm, "mid": v(32.75, -38.5) * mm, "end": v(28.75, -34.5) * mm});
            skArc(sketch, "E166.2.0.7", {"start": v(36.75, 3.5) * mm, "mid": v(32.75, -0.5) * mm, "end": v(28.75, 3.5) * mm});
            skLineSegment(sketch, "E166.2.0.11", {"start": v(32.75, -10.5) * mm, "end": v(32.75, -34.5) * mm, "construction": true});
            skLineSegment(sketch, "E166.2.0.12", {"start": v(32.75, 3.5) * mm, "end": v(32.75, -10.5) * mm, "construction": true});
            skLineSegment(sketch, "E166.2.0.13", {"start": v(32.75, 27.5) * mm, "end": v(32.75, 3.5) * mm, "construction": true});
            skLineSegment(sketch, "E166.2.0.14", {"start": v(32.75, 41.5) * mm, "end": v(32.75, 27.5) * mm, "construction": true});
            skLineSegment(sketch, "E166.2.0.15", {"start": v(32.75, 65.5) * mm, "end": v(32.75, 41.5) * mm, "construction": true});
            skLineSegment(sketch, "E166.2.0.16", {"start": v(36.75, 27.5) * mm, "end": v(36.75, 3.5) * mm});
            skLineSegment(sketch, "E166.2.0.20", {"start": v(28.75, 65.5) * mm, "end": v(28.75, 41.5) * mm});
            skLineSegment(sketch, "E166.2.0.21", {"start": v(36.75, 65.5) * mm, "end": v(36.75, 41.5) * mm});
            skArc(sketch, "E166.2.0.22", {"start": v(36.75, 41.5) * mm, "mid": v(32.75, 37.5) * mm, "end": v(28.75, 41.5) * mm});
            skLineSegment(sketch, "E166.2.0.23", {"start": v(36.75, -10.5) * mm, "end": v(36.75, -34.5) * mm});
            skLineSegment(sketch, "E166.direction1", {"start": v(-7.25, -34.5) * mm, "end": v(10.75, -34.5) * mm, "construction": true});
            skLineSegment(sketch, "E167", {"start": v(-7.75, 109) * mm, "end": v(19.75, 109) * mm});
            skLineSegment(sketch, "E168", {"start": v(-7.75, 109) * mm, "end": v(-7.75, 96) * mm});
            skLineSegment(sketch, "E169", {"start": v(-7.75, 96) * mm, "end": v(-7.75, 89.2) * mm, "construction": true});
            skLineSegment(sketch, "E170", {"start": v(-7.75, 89.2) * mm, "end": v(-2, 89.2) * mm, "construction": true});
            skLineSegment(sketch, "E171", {"start": v(-2, 89.2) * mm, "end": v(14, 89.2) * mm});
            skLineSegment(sketch, "E172", {"start": v(14, 89.2) * mm, "end": v(19.75, 89.2) * mm, "construction": true});
            skLineSegment(sketch, "E173", {"start": v(19.75, 89.2) * mm, "end": v(19.75, 96) * mm, "construction": true});
            skLineSegment(sketch, "E174", {"start": v(19.75, 96) * mm, "end": v(19.75, 109) * mm});
            skLineSegment(sketch, "E175", {"start": v(-7.75, 96) * mm, "end": v(-2, 89.2) * mm});
            skLineSegment(sketch, "E176", {"start": v(14, 89.2) * mm, "end": v(19.75, 96) * mm});
            skLineSegment(sketch, "E177", {"start": v(6, 89.2) * mm, "end": v(6, 109) * mm, "construction": true});
            skLineSegment(sketch, "E178", {"start": v(19.75, 99.6) * mm, "end": v(25.95, 99.6) * mm, "construction": true});
            skLineSegment(sketch, "E179", {"start": v(-7.75, 100) * mm, "end": v(-13.95, 100) * mm, "construction": true});
            skCircle(sketch, "E180", {"center": v(25.95, 99.6) * mm, "radius": 1.5 * mm});
            skCircle(sketch, "E181", {"center": v(-13.95, 100) * mm, "radius": 1.5 * mm});
            skLineSegment(sketch, "E182", {"start": v(6, 109) * mm, "end": v(6, 119) * mm, "construction": true});
            skLineSegment(sketch, "E183", {"start": v(48, 119) * mm, "end": v(48, 101) * mm, "construction": true});
            skLineSegment(sketch, "E184", {"start": v(48, 101) * mm, "end": v(66, 101) * mm, "construction": true});
            skCircle(sketch, "E185", {"center": v(48, 101) * mm, "radius": 6 * mm});
            skSolve(sketch);
        }
        {
            var Q0;
            Q0=qSketchRegion(id+"F31",true);
            var Q1;
            Q1=qSketchRegion(id+"F32",true);
            extrude(context, id + "F33", {"entities" : qUnion([Q0, Q1]), "operationType" : NewBodyOperationType.REMOVE, "oppositeDirection" : true, "depth" : 25 * mm});
        }
        {
            var Q0;
            Q0=makeQuery(id+"F33.boolean.opBoolean","COPY",EDGE,{"derivedFrom":makeQuery(id+"F33.opExtrude","SWEPT_EDGE",EDGE,{"disambiguationData":[OSD([sQuery(id+"F31.wireOp",EDGE,"E140.top"),sQuery(id+"F31.wireOp",EDGE,"E140.left")])]})});
            var Q1;
            Q1=makeQuery(id+"F33.boolean.opBoolean","COPY",EDGE,{"derivedFrom":makeQuery(id+"F33.opExtrude","SWEPT_EDGE",EDGE,{"disambiguationData":[OSD([sQuery(id+"F31.wireOp",EDGE,"E140.bottom"),sQuery(id+"F31.wireOp",EDGE,"E140.left")])]})});
            var Q2;
            Q2=makeQuery(id+"F33.boolean.opBoolean","COPY",EDGE,{"derivedFrom":makeQuery(id+"F33.opExtrude","SWEPT_EDGE",EDGE,{"disambiguationData":[OSD([sQuery(id+"F31.wireOp",EDGE,"E141.bottom"),sQuery(id+"F31.wireOp",EDGE,"E141.left")])]})});
            var Q3;
            Q3=makeQuery(id+"F33.boolean.opBoolean","COPY",EDGE,{"derivedFrom":makeQuery(id+"F33.opExtrude","SWEPT_EDGE",EDGE,{"disambiguationData":[OSD([sQuery(id+"F31.wireOp",EDGE,"E141.top"),sQuery(id+"F31.wireOp",EDGE,"E141.left")])]})});
            var Q4;
            Q4=makeQuery(id+"F33.boolean.opBoolean","COPY",EDGE,{"derivedFrom":makeQuery(id+"F33.opExtrude","SWEPT_EDGE",EDGE,{"disambiguationData":[OSD([sQuery(id+"F31.wireOp",EDGE,"E141.top"),sQuery(id+"F31.wireOp",EDGE,"E141.right")])]})});
            var Q5;
            Q5=makeQuery(id+"F33.boolean.opBoolean","COPY",EDGE,{"derivedFrom":makeQuery(id+"F33.opExtrude","SWEPT_EDGE",EDGE,{"disambiguationData":[OSD([sQuery(id+"F31.wireOp",EDGE,"E141.bottom"),sQuery(id+"F31.wireOp",EDGE,"E141.right")])]})});
            var Q6;
            Q6=makeQuery(id+"F33.boolean.opBoolean","COPY",EDGE,{"derivedFrom":makeQuery(id+"F33.opExtrude","SWEPT_EDGE",EDGE,{"disambiguationData":[OSD([sQuery(id+"F31.wireOp",EDGE,"E140.bottom"),sQuery(id+"F31.wireOp",EDGE,"E140.right")])]})});
            var Q7;
            Q7=makeQuery(id+"F33.boolean.opBoolean","COPY",EDGE,{"derivedFrom":makeQuery(id+"F33.opExtrude","SWEPT_EDGE",EDGE,{"disambiguationData":[OSD([sQuery(id+"F31.wireOp",EDGE,"E140.top"),sQuery(id+"F31.wireOp",EDGE,"E140.right")])]})});
            chamfer(context, id + "F34", {"entities" : qUnion([Q0, Q1, Q2, Q3, Q4, Q5, Q6, Q7]), "width" : 2 * mm, "tangentPropagation" : true});
        }
        {
            var Q0;
            {var subQ0=makeQuery(id+"F19.opExtrude","CAP_FACE",FACE,{"disambiguationData":[OSD([sQuery(id+"F18.wireOp",EDGE,"E100.bottom"),sQuery(id+"F18.wireOp",EDGE,"E100.top"),sQuery(id+"F18.wireOp",EDGE,"E100.left"),sQuery(id+"F18.wireOp",EDGE,"E100.right"),sQuery(id+"F18.wireOp",EDGE,"E101"),sQuery(id+"F18.wireOp",EDGE,"E102"),sQuery(id+"F18.wireOp",EDGE,"E103"),sQuery(id+"F18.wireOp",EDGE,"E104")])],"isStart":false});Q0=makeQuery(id+"F20.boolean.opBoolean","MERGE",FACE,{"derivedFrom":[subQ0,makeQuery(id+"F20.opPattern","COPY",FACE,{"derivedFrom":subQ0,"instanceName":"1"})]});}
            var sketch = newSketch(context, id + "F35", { "sketchPlane" : qUnion([Q0])});
            skLineSegment(sketch, "E186", {"start": v(24.98, 239.87) * mm, "end": v(24.98, 224.87) * mm, "construction": true});
            skLineSegment(sketch, "E187", {"start": v(24.98, 224.87) * mm, "end": v(39.98, 224.87) * mm, "construction": true});
            skArc(sketch, "E188.0.startCap", {"start": v(24.98, 222.37) * mm, "mid": v(22.48, 224.87) * mm, "end": v(24.98, 227.37) * mm});
            skArc(sketch, "E188.0.endCap", {"start": v(39.98, 227.37) * mm, "mid": v(42.48, 224.87) * mm, "end": v(39.98, 222.37) * mm});
            skLineSegment(sketch, "E188.0.left", {"start": v(24.98, 227.37) * mm, "end": v(39.98, 227.37) * mm});
            skLineSegment(sketch, "E188.0.right", {"start": v(24.98, 222.37) * mm, "end": v(39.98, 222.37) * mm});
            skLineSegment(sketch, "E189.0.1.0", {"start": v(24.98, 212.37) * mm, "end": v(39.98, 212.37) * mm});
            skLineSegment(sketch, "E189.0.1.1", {"start": v(24.98, 217.37) * mm, "end": v(39.98, 217.37) * mm});
            skArc(sketch, "E189.0.1.2", {"start": v(24.98, 212.37) * mm, "mid": v(22.48, 214.87) * mm, "end": v(24.98, 217.37) * mm});
            skLineSegment(sketch, "E189.0.1.3", {"start": v(24.98, 214.87) * mm, "end": v(39.98, 214.87) * mm, "construction": true});
            skArc(sketch, "E189.0.1.4", {"start": v(39.98, 217.37) * mm, "mid": v(42.48, 214.87) * mm, "end": v(39.98, 212.37) * mm});
            skLineSegment(sketch, "E189.0.2.0", {"start": v(24.98, 202.37) * mm, "end": v(39.98, 202.37) * mm});
            skLineSegment(sketch, "E189.0.2.1", {"start": v(24.98, 207.37) * mm, "end": v(39.98, 207.37) * mm});
            skArc(sketch, "E189.0.2.2", {"start": v(24.98, 202.37) * mm, "mid": v(22.48, 204.87) * mm, "end": v(24.98, 207.37) * mm});
            skLineSegment(sketch, "E189.0.2.3", {"start": v(24.98, 204.87) * mm, "end": v(39.98, 204.87) * mm, "construction": true});
            skArc(sketch, "E189.0.2.4", {"start": v(39.98, 207.37) * mm, "mid": v(42.48, 204.87) * mm, "end": v(39.98, 202.37) * mm});
            skLineSegment(sketch, "E189.0.3.0", {"start": v(24.98, 192.37) * mm, "end": v(39.98, 192.37) * mm});
            skLineSegment(sketch, "E189.0.3.1", {"start": v(24.98, 197.37) * mm, "end": v(39.98, 197.37) * mm});
            skArc(sketch, "E189.0.3.2", {"start": v(24.98, 192.37) * mm, "mid": v(22.48, 194.87) * mm, "end": v(24.98, 197.37) * mm});
            skLineSegment(sketch, "E189.0.3.3", {"start": v(24.98, 194.87) * mm, "end": v(39.98, 194.87) * mm, "construction": true});
            skArc(sketch, "E189.0.3.4", {"start": v(39.98, 197.37) * mm, "mid": v(42.48, 194.87) * mm, "end": v(39.98, 192.37) * mm});
            skLineSegment(sketch, "E189.0.4.0", {"start": v(24.98, 182.37) * mm, "end": v(39.98, 182.37) * mm});
            skLineSegment(sketch, "E189.0.4.1", {"start": v(24.98, 187.37) * mm, "end": v(39.98, 187.37) * mm});
            skArc(sketch, "E189.0.4.2", {"start": v(24.98, 182.37) * mm, "mid": v(22.48, 184.87) * mm, "end": v(24.98, 187.37) * mm});
            skLineSegment(sketch, "E189.0.4.3", {"start": v(24.98, 184.87) * mm, "end": v(39.98, 184.87) * mm, "construction": true});
            skArc(sketch, "E189.0.4.4", {"start": v(39.98, 187.37) * mm, "mid": v(42.48, 184.87) * mm, "end": v(39.98, 182.37) * mm});
            skLineSegment(sketch, "E189.0.5.0", {"start": v(24.98, 172.37) * mm, "end": v(39.98, 172.37) * mm});
            skLineSegment(sketch, "E189.0.5.1", {"start": v(24.98, 177.37) * mm, "end": v(39.98, 177.37) * mm});
            skArc(sketch, "E189.0.5.2", {"start": v(24.98, 172.37) * mm, "mid": v(22.48, 174.87) * mm, "end": v(24.98, 177.37) * mm});
            skLineSegment(sketch, "E189.0.5.3", {"start": v(24.98, 174.87) * mm, "end": v(39.98, 174.87) * mm, "construction": true});
            skArc(sketch, "E189.0.5.4", {"start": v(39.98, 177.37) * mm, "mid": v(42.48, 174.87) * mm, "end": v(39.98, 172.37) * mm});
            skLineSegment(sketch, "E189.0.6.0", {"start": v(24.98, 162.37) * mm, "end": v(39.98, 162.37) * mm});
            skLineSegment(sketch, "E189.0.6.1", {"start": v(24.98, 167.37) * mm, "end": v(39.98, 167.37) * mm});
            skArc(sketch, "E189.0.6.2", {"start": v(24.98, 162.37) * mm, "mid": v(22.48, 164.87) * mm, "end": v(24.98, 167.37) * mm});
            skLineSegment(sketch, "E189.0.6.3", {"start": v(24.98, 164.87) * mm, "end": v(39.98, 164.87) * mm, "construction": true});
            skArc(sketch, "E189.0.6.4", {"start": v(39.98, 167.37) * mm, "mid": v(42.48, 164.87) * mm, "end": v(39.98, 162.37) * mm});
            skLineSegment(sketch, "E189.0.7.0", {"start": v(24.98, 152.37) * mm, "end": v(39.98, 152.37) * mm});
            skLineSegment(sketch, "E189.0.7.1", {"start": v(24.98, 157.37) * mm, "end": v(39.98, 157.37) * mm});
            skArc(sketch, "E189.0.7.2", {"start": v(24.98, 152.37) * mm, "mid": v(22.48, 154.87) * mm, "end": v(24.98, 157.37) * mm});
            skLineSegment(sketch, "E189.0.7.3", {"start": v(24.98, 154.87) * mm, "end": v(39.98, 154.87) * mm, "construction": true});
            skArc(sketch, "E189.0.7.4", {"start": v(39.98, 157.37) * mm, "mid": v(42.48, 154.87) * mm, "end": v(39.98, 152.37) * mm});
            skLineSegment(sketch, "E189.0.8.0", {"start": v(24.98, 142.37) * mm, "end": v(39.98, 142.37) * mm});
            skLineSegment(sketch, "E189.0.8.1", {"start": v(24.98, 147.37) * mm, "end": v(39.98, 147.37) * mm});
            skArc(sketch, "E189.0.8.2", {"start": v(24.98, 142.37) * mm, "mid": v(22.48, 144.87) * mm, "end": v(24.98, 147.37) * mm});
            skLineSegment(sketch, "E189.0.8.3", {"start": v(24.98, 144.87) * mm, "end": v(39.98, 144.87) * mm, "construction": true});
            skArc(sketch, "E189.0.8.4", {"start": v(39.98, 147.37) * mm, "mid": v(42.48, 144.87) * mm, "end": v(39.98, 142.37) * mm});
            skLineSegment(sketch, "E189.0.9.0", {"start": v(24.98, 132.37) * mm, "end": v(39.98, 132.37) * mm});
            skLineSegment(sketch, "E189.0.9.1", {"start": v(24.98, 137.37) * mm, "end": v(39.98, 137.37) * mm});
            skArc(sketch, "E189.0.9.2", {"start": v(24.98, 132.37) * mm, "mid": v(22.48, 134.87) * mm, "end": v(24.98, 137.37) * mm});
            skLineSegment(sketch, "E189.0.9.3", {"start": v(24.98, 134.87) * mm, "end": v(39.98, 134.87) * mm, "construction": true});
            skArc(sketch, "E189.0.9.4", {"start": v(39.98, 137.37) * mm, "mid": v(42.48, 134.87) * mm, "end": v(39.98, 132.37) * mm});
            skLineSegment(sketch, "E189.0.10.0", {"start": v(24.98, 122.37) * mm, "end": v(39.98, 122.37) * mm});
            skLineSegment(sketch, "E189.0.10.1", {"start": v(24.98, 127.37) * mm, "end": v(39.98, 127.37) * mm});
            skArc(sketch, "E189.0.10.2", {"start": v(24.98, 122.37) * mm, "mid": v(22.48, 124.87) * mm, "end": v(24.98, 127.37) * mm});
            skLineSegment(sketch, "E189.0.10.3", {"start": v(24.98, 124.87) * mm, "end": v(39.98, 124.87) * mm, "construction": true});
            skArc(sketch, "E189.0.10.4", {"start": v(39.98, 127.37) * mm, "mid": v(42.48, 124.87) * mm, "end": v(39.98, 122.37) * mm});
            skLineSegment(sketch, "E189.0.11.0", {"start": v(24.98, 112.37) * mm, "end": v(39.98, 112.37) * mm});
            skLineSegment(sketch, "E189.0.11.1", {"start": v(24.98, 117.37) * mm, "end": v(39.98, 117.37) * mm});
            skArc(sketch, "E189.0.11.2", {"start": v(24.98, 112.37) * mm, "mid": v(22.48, 114.87) * mm, "end": v(24.98, 117.37) * mm});
            skLineSegment(sketch, "E189.0.11.3", {"start": v(24.98, 114.87) * mm, "end": v(39.98, 114.87) * mm, "construction": true});
            skArc(sketch, "E189.0.11.4", {"start": v(39.98, 117.37) * mm, "mid": v(42.48, 114.87) * mm, "end": v(39.98, 112.37) * mm});
            skLineSegment(sketch, "E189.0.12.0", {"start": v(24.98, 102.37) * mm, "end": v(39.98, 102.37) * mm});
            skLineSegment(sketch, "E189.0.12.1", {"start": v(24.98, 107.37) * mm, "end": v(39.98, 107.37) * mm});
            skArc(sketch, "E189.0.12.2", {"start": v(24.98, 102.37) * mm, "mid": v(22.48, 104.87) * mm, "end": v(24.98, 107.37) * mm});
            skLineSegment(sketch, "E189.0.12.3", {"start": v(24.98, 104.87) * mm, "end": v(39.98, 104.87) * mm, "construction": true});
            skArc(sketch, "E189.0.12.4", {"start": v(39.98, 107.37) * mm, "mid": v(42.48, 104.87) * mm, "end": v(39.98, 102.37) * mm});
            skLineSegment(sketch, "E189.0.13.0", {"start": v(24.98, 92.37) * mm, "end": v(39.98, 92.37) * mm});
            skLineSegment(sketch, "E189.0.13.1", {"start": v(24.98, 97.37) * mm, "end": v(39.98, 97.37) * mm});
            skArc(sketch, "E189.0.13.2", {"start": v(24.98, 92.37) * mm, "mid": v(22.48, 94.87) * mm, "end": v(24.98, 97.37) * mm});
            skLineSegment(sketch, "E189.0.13.3", {"start": v(24.98, 94.87) * mm, "end": v(39.98, 94.87) * mm, "construction": true});
            skArc(sketch, "E189.0.13.4", {"start": v(39.98, 97.37) * mm, "mid": v(42.48, 94.87) * mm, "end": v(39.98, 92.37) * mm});
            skLineSegment(sketch, "E189.0.14.0", {"start": v(24.98, 82.37) * mm, "end": v(39.98, 82.37) * mm});
            skLineSegment(sketch, "E189.0.14.1", {"start": v(24.98, 87.37) * mm, "end": v(39.98, 87.37) * mm});
            skArc(sketch, "E189.0.14.2", {"start": v(24.98, 82.37) * mm, "mid": v(22.48, 84.87) * mm, "end": v(24.98, 87.37) * mm});
            skLineSegment(sketch, "E189.0.14.3", {"start": v(24.98, 84.87) * mm, "end": v(39.98, 84.87) * mm, "construction": true});
            skArc(sketch, "E189.0.14.4", {"start": v(39.98, 87.37) * mm, "mid": v(42.48, 84.87) * mm, "end": v(39.98, 82.37) * mm});
            skLineSegment(sketch, "E189.direction1", {"start": v(-46.02, 222.37) * mm, "end": v(24.98, 222.37) * mm, "construction": true});
            skLineSegment(sketch, "E189.direction2", {"start": v(24.98, 222.37) * mm, "end": v(24.98, 212.37) * mm, "construction": true});
            skSolve(sketch);
        }
        {
            var Q0;
            Q0=qSketchRegion(id+"F35",true);
            extrude(context, id + "F36", {"entities" : qUnion([Q0]), "operationType" : NewBodyOperationType.REMOVE, "oppositeDirection" : true, "depth" : 25 * mm});
        }
    });
